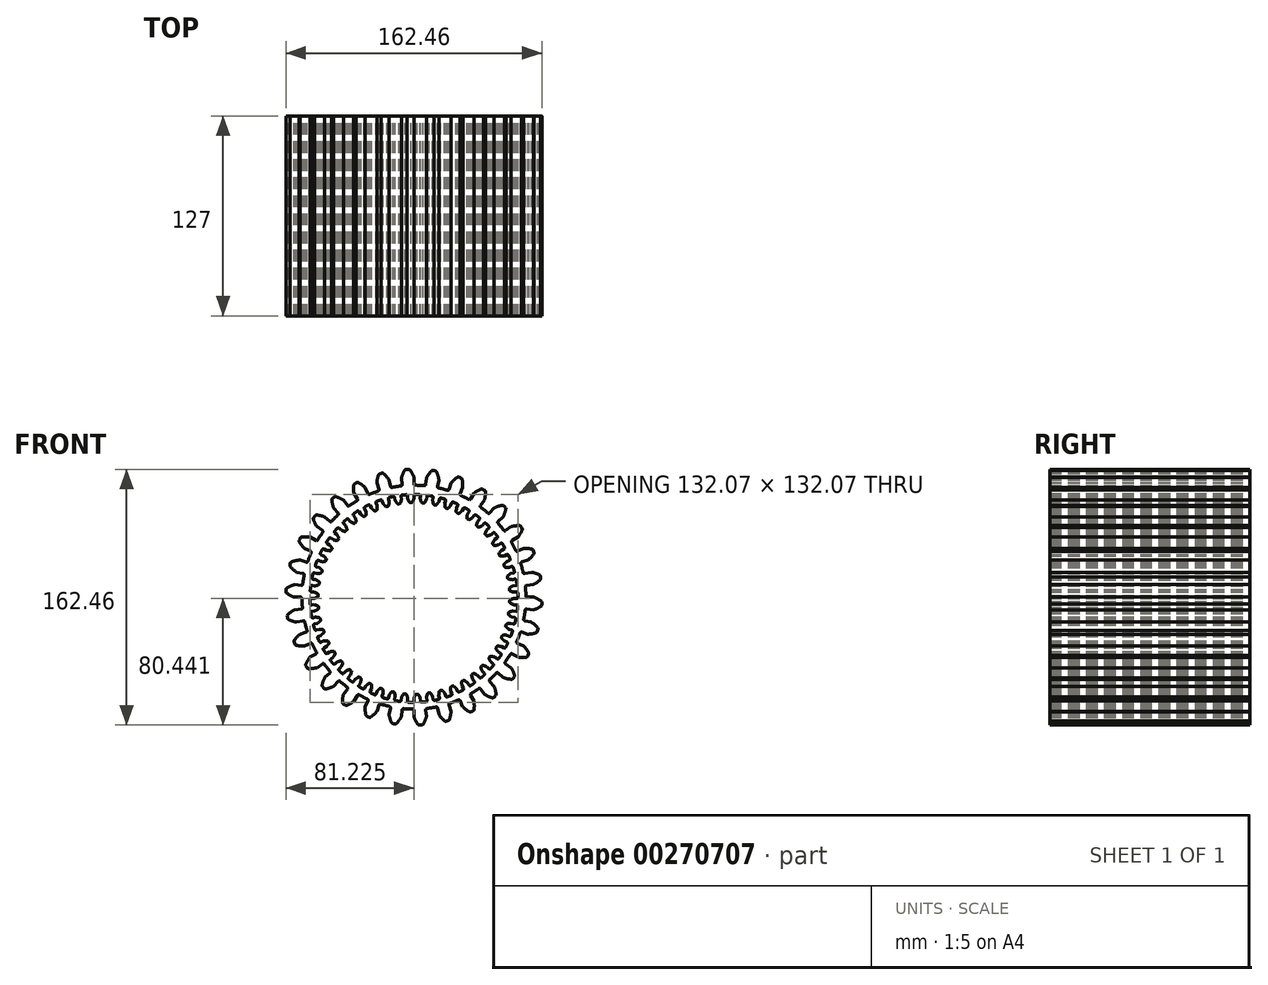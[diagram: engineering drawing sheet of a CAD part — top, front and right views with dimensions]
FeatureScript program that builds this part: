
annotation { "Feature Type Name" : "Feature", "Feature Type Description" : "" }
export const myFeature = defineFeature(function(context is Context, id is Id, definition is map)
    precondition{}
    {
        {
            var Q0;
            Q0=qCreatedBy(makeId("Front.planeOp"),FACE);
            var sketch = newSketch(context, id + "F0", { "sketchPlane" : qUnion([Q0])});
            skArc(sketch, "E0", {"start": v(-8.2, 70.64) * mm, "mid": v(-11.13, 70.24) * mm, "end": v(-14.02, 69.72) * mm});
            skArc(sketch, "E1.trimOffspring", {"start": v(0, 76.2) * mm, "mid": v(-1.16, 78.65) * mm, "end": v(-2.65, 80.92) * mm});
            skLineSegment(sketch, "E2", {"start": v(-3.27, 81.23) * mm, "end": v(-4.26, 81.23) * mm});
            skLineSegment(sketch, "E3", {"start": v(0, 76.2) * mm, "end": v(0, 71.9) * mm});
            skLineSegment(sketch, "E4.MirrorCS", {"start": v(-5.24, 81.13) * mm, "end": v(-4.26, 81.23) * mm});
            skArc(sketch, "E5.MirrorCS", {"start": v(-7.97, 75.78) * mm, "mid": v(-7.07, 78.34) * mm, "end": v(-5.83, 80.75) * mm});
            skLineSegment(sketch, "E6.MirrorCS", {"start": v(-7.97, 75.78) * mm, "end": v(-7.52, 71.5) * mm});
            skPoint(sketch, "E7.visualSharp", {"position": v(0, 71.12) * mm});
            skArc(sketch, "E7.filletArc", {"start": v(0, 71.9) * mm, "mid": v(0.23, 71.35) * mm, "end": v(0.78, 71.12) * mm});
            skPoint(sketch, "E8.visualSharp", {"position": v(-7.43, 70.73) * mm});
            skArc(sketch, "E8.filletArc", {"start": v(-8.2, 70.64) * mm, "mid": v(-7.68, 70.93) * mm, "end": v(-7.52, 71.5) * mm});
            skPoint(sketch, "E9.visualSharp", {"position": v(-5.62, 81.09) * mm});
            skArc(sketch, "E9.filletArc", {"start": v(-5.24, 81.13) * mm, "mid": v(-5.57, 81) * mm, "end": v(-5.83, 80.75) * mm});
            skPoint(sketch, "E10.visualSharp", {"position": v(-2.89, 81.23) * mm});
            skArc(sketch, "E10.filletArc", {"start": v(-2.65, 80.92) * mm, "mid": v(-2.92, 81.15) * mm, "end": v(-3.27, 81.23) * mm});
            skArc(sketch, "E11.1.0", {"start": v(-22.72, 67.4) * mm, "mid": v(-22.26, 67.79) * mm, "end": v(-22.22, 68.38) * mm});
            skLineSegment(sketch, "E11.1.1", {"start": v(-23.55, 72.47) * mm, "end": v(-22.22, 68.38) * mm});
            skArc(sketch, "E11.1.2", {"start": v(-23.55, 72.47) * mm, "mid": v(-23.2, 75.16) * mm, "end": v(-22.49, 77.78) * mm});
            skArc(sketch, "E11.1.3", {"start": v(-21.99, 78.26) * mm, "mid": v(-22.3, 78.08) * mm, "end": v(-22.49, 77.78) * mm});
            skLineSegment(sketch, "E11.1.4", {"start": v(-21.99, 78.26) * mm, "end": v(-21.05, 78.57) * mm});
            skLineSegment(sketch, "E11.1.5", {"start": v(-20.09, 78.77) * mm, "end": v(-21.05, 78.57) * mm});
            skArc(sketch, "E11.1.6", {"start": v(-19.41, 78.6) * mm, "mid": v(-19.73, 78.77) * mm, "end": v(-20.09, 78.77) * mm});
            skArc(sketch, "E11.1.7", {"start": v(-15.84, 74.53) * mm, "mid": v(-17.48, 76.7) * mm, "end": v(-19.41, 78.6) * mm});
            skLineSegment(sketch, "E11.1.8", {"start": v(-15.84, 74.53) * mm, "end": v(-14.95, 70.33) * mm});
            skArc(sketch, "E11.1.9", {"start": v(-14.95, 70.33) * mm, "mid": v(-14.61, 69.84) * mm, "end": v(-14.02, 69.72) * mm});
            skArc(sketch, "E11.2.0", {"start": v(-36.23, 61.2) * mm, "mid": v(-35.87, 61.68) * mm, "end": v(-35.95, 62.27) * mm});
            skLineSegment(sketch, "E11.2.1", {"start": v(-38.1, 66) * mm, "end": v(-35.95, 62.27) * mm});
            skArc(sketch, "E11.2.2", {"start": v(-38.1, 66) * mm, "mid": v(-38.33, 68.7) * mm, "end": v(-38.17, 71.4) * mm});
            skArc(sketch, "E11.2.3", {"start": v(-37.78, 71.98) * mm, "mid": v(-38.04, 71.74) * mm, "end": v(-38.17, 71.4) * mm});
            skLineSegment(sketch, "E11.2.4", {"start": v(-37.78, 71.98) * mm, "end": v(-36.93, 72.47) * mm});
            skLineSegment(sketch, "E11.2.5", {"start": v(-36.03, 72.87) * mm, "end": v(-36.93, 72.47) * mm});
            skArc(sketch, "E11.2.6", {"start": v(-35.33, 72.85) * mm, "mid": v(-35.68, 72.94) * mm, "end": v(-36.03, 72.87) * mm});
            skArc(sketch, "E11.2.7", {"start": v(-31, 69.61) * mm, "mid": v(-33.05, 71.38) * mm, "end": v(-35.33, 72.85) * mm});
            skLineSegment(sketch, "E11.2.8", {"start": v(-31, 69.61) * mm, "end": v(-29.25, 65.69) * mm});
            skArc(sketch, "E11.2.9", {"start": v(-29.25, 65.69) * mm, "mid": v(-28.81, 65.27) * mm, "end": v(-28.21, 65.28) * mm});
            skArc(sketch, "E11.3.0", {"start": v(-48.16, 52.33) * mm, "mid": v(-47.91, 52.87) * mm, "end": v(-48.11, 53.43) * mm});
            skLineSegment(sketch, "E11.3.1", {"start": v(-50.99, 56.63) * mm, "end": v(-48.11, 53.43) * mm});
            skArc(sketch, "E11.3.2", {"start": v(-50.99, 56.63) * mm, "mid": v(-51.77, 59.22) * mm, "end": v(-52.18, 61.9) * mm});
            skArc(sketch, "E11.3.3", {"start": v(-51.92, 62.55) * mm, "mid": v(-52.12, 62.26) * mm, "end": v(-52.18, 61.9) * mm});
            skLineSegment(sketch, "E11.3.4", {"start": v(-51.92, 62.55) * mm, "end": v(-51.19, 63.21) * mm});
            skLineSegment(sketch, "E11.3.5", {"start": v(-50.4, 63.8) * mm, "end": v(-51.19, 63.21) * mm});
            skArc(sketch, "E11.3.6", {"start": v(-49.7, 63.9) * mm, "mid": v(-50.06, 63.93) * mm, "end": v(-50.4, 63.8) * mm});
            skArc(sketch, "E11.3.7", {"start": v(-44.79, 61.65) * mm, "mid": v(-47.17, 62.95) * mm, "end": v(-49.7, 63.9) * mm});
            skLineSegment(sketch, "E11.3.8", {"start": v(-44.79, 61.65) * mm, "end": v(-42.26, 58.17) * mm});
            skArc(sketch, "E11.3.9", {"start": v(-42.26, 58.17) * mm, "mid": v(-41.75, 57.86) * mm, "end": v(-41.17, 58) * mm});
            skArc(sketch, "E11.4.0", {"start": v(-58, 41.17) * mm, "mid": v(-57.86, 41.75) * mm, "end": v(-58.17, 42.26) * mm});
            skLineSegment(sketch, "E11.4.1", {"start": v(-61.65, 44.79) * mm, "end": v(-58.17, 42.26) * mm});
            skArc(sketch, "E11.4.2", {"start": v(-61.65, 44.79) * mm, "mid": v(-62.95, 47.17) * mm, "end": v(-63.9, 49.7) * mm});
            skArc(sketch, "E11.4.3", {"start": v(-63.8, 50.4) * mm, "mid": v(-63.93, 50.06) * mm, "end": v(-63.9, 49.7) * mm});
            skLineSegment(sketch, "E11.4.4", {"start": v(-63.8, 50.4) * mm, "end": v(-63.21, 51.19) * mm});
            skLineSegment(sketch, "E11.4.5", {"start": v(-62.55, 51.92) * mm, "end": v(-63.21, 51.19) * mm});
            skArc(sketch, "E11.4.6", {"start": v(-61.9, 52.18) * mm, "mid": v(-62.26, 52.12) * mm, "end": v(-62.55, 51.92) * mm});
            skArc(sketch, "E11.4.7", {"start": v(-56.63, 50.99) * mm, "mid": v(-59.22, 51.77) * mm, "end": v(-61.9, 52.18) * mm});
            skLineSegment(sketch, "E11.4.8", {"start": v(-56.63, 50.99) * mm, "end": v(-53.43, 48.11) * mm});
            skArc(sketch, "E11.4.9", {"start": v(-53.43, 48.11) * mm, "mid": v(-52.87, 47.91) * mm, "end": v(-52.33, 48.16) * mm});
            skArc(sketch, "E11.5.0", {"start": v(-65.28, 28.21) * mm, "mid": v(-65.27, 28.81) * mm, "end": v(-65.69, 29.25) * mm});
            skLineSegment(sketch, "E11.5.1", {"start": v(-69.61, 31) * mm, "end": v(-65.69, 29.25) * mm});
            skArc(sketch, "E11.5.2", {"start": v(-69.61, 31) * mm, "mid": v(-71.38, 33.05) * mm, "end": v(-72.85, 35.33) * mm});
            skArc(sketch, "E11.5.3", {"start": v(-72.87, 36.03) * mm, "mid": v(-72.94, 35.68) * mm, "end": v(-72.85, 35.33) * mm});
            skLineSegment(sketch, "E11.5.4", {"start": v(-72.87, 36.03) * mm, "end": v(-72.47, 36.93) * mm});
            skLineSegment(sketch, "E11.5.5", {"start": v(-71.98, 37.78) * mm, "end": v(-72.47, 36.93) * mm});
            skArc(sketch, "E11.5.6", {"start": v(-71.4, 38.17) * mm, "mid": v(-71.74, 38.04) * mm, "end": v(-71.98, 37.78) * mm});
            skArc(sketch, "E11.5.7", {"start": v(-66, 38.1) * mm, "mid": v(-68.7, 38.33) * mm, "end": v(-71.4, 38.17) * mm});
            skLineSegment(sketch, "E11.5.8", {"start": v(-66, 38.1) * mm, "end": v(-62.27, 35.95) * mm});
            skArc(sketch, "E11.5.9", {"start": v(-62.27, 35.95) * mm, "mid": v(-61.68, 35.87) * mm, "end": v(-61.2, 36.23) * mm});
            skArc(sketch, "E11.6.0", {"start": v(-69.72, 14.02) * mm, "mid": v(-69.84, 14.61) * mm, "end": v(-70.33, 14.95) * mm});
            skLineSegment(sketch, "E11.6.1", {"start": v(-74.53, 15.84) * mm, "end": v(-70.33, 14.95) * mm});
            skArc(sketch, "E11.6.2", {"start": v(-74.53, 15.84) * mm, "mid": v(-76.7, 17.48) * mm, "end": v(-78.6, 19.41) * mm});
            skArc(sketch, "E11.6.3", {"start": v(-78.77, 20.09) * mm, "mid": v(-78.77, 19.73) * mm, "end": v(-78.6, 19.41) * mm});
            skLineSegment(sketch, "E11.6.4", {"start": v(-78.77, 20.09) * mm, "end": v(-78.57, 21.05) * mm});
            skLineSegment(sketch, "E11.6.5", {"start": v(-78.26, 21.99) * mm, "end": v(-78.57, 21.05) * mm});
            skArc(sketch, "E11.6.6", {"start": v(-77.78, 22.49) * mm, "mid": v(-78.08, 22.3) * mm, "end": v(-78.26, 21.99) * mm});
            skArc(sketch, "E11.6.7", {"start": v(-72.47, 23.55) * mm, "mid": v(-75.16, 23.2) * mm, "end": v(-77.78, 22.49) * mm});
            skLineSegment(sketch, "E11.6.8", {"start": v(-72.47, 23.55) * mm, "end": v(-68.38, 22.22) * mm});
            skArc(sketch, "E11.6.9", {"start": v(-68.38, 22.22) * mm, "mid": v(-67.79, 22.26) * mm, "end": v(-67.4, 22.72) * mm});
            skArc(sketch, "E11.7.0", {"start": v(-71.12, -0.78) * mm, "mid": v(-71.35, -0.23) * mm, "end": v(-71.9, 0) * mm});
            skLineSegment(sketch, "E11.7.1", {"start": v(-76.2, 0) * mm, "end": v(-71.9, 0) * mm});
            skArc(sketch, "E11.7.2", {"start": v(-76.2, 0) * mm, "mid": v(-78.65, 1.16) * mm, "end": v(-80.92, 2.65) * mm});
            skArc(sketch, "E11.7.3", {"start": v(-81.23, 3.27) * mm, "mid": v(-81.15, 2.92) * mm, "end": v(-80.92, 2.65) * mm});
            skLineSegment(sketch, "E11.7.4", {"start": v(-81.23, 3.27) * mm, "end": v(-81.23, 4.26) * mm});
            skLineSegment(sketch, "E11.7.5", {"start": v(-81.13, 5.24) * mm, "end": v(-81.23, 4.26) * mm});
            skArc(sketch, "E11.7.6", {"start": v(-80.75, 5.83) * mm, "mid": v(-81, 5.57) * mm, "end": v(-81.13, 5.24) * mm});
            skArc(sketch, "E11.7.7", {"start": v(-75.78, 7.97) * mm, "mid": v(-78.34, 7.07) * mm, "end": v(-80.75, 5.83) * mm});
            skLineSegment(sketch, "E11.7.8", {"start": v(-75.78, 7.97) * mm, "end": v(-71.5, 7.52) * mm});
            skArc(sketch, "E11.7.9", {"start": v(-71.5, 7.52) * mm, "mid": v(-70.93, 7.68) * mm, "end": v(-70.64, 8.2) * mm});
            skArc(sketch, "E11.8.0", {"start": v(-69.4, -15.55) * mm, "mid": v(-69.74, -15.06) * mm, "end": v(-70.33, -14.95) * mm});
            skLineSegment(sketch, "E11.8.1", {"start": v(-74.53, -15.84) * mm, "end": v(-70.33, -14.95) * mm});
            skArc(sketch, "E11.8.2", {"start": v(-74.53, -15.84) * mm, "mid": v(-77.18, -15.22) * mm, "end": v(-79.7, -14.23) * mm});
            skArc(sketch, "E11.8.3", {"start": v(-80.13, -13.69) * mm, "mid": v(-79.98, -14.01) * mm, "end": v(-79.7, -14.23) * mm});
            skLineSegment(sketch, "E11.8.4", {"start": v(-80.13, -13.69) * mm, "end": v(-80.34, -12.72) * mm});
            skLineSegment(sketch, "E11.8.5", {"start": v(-80.44, -11.75) * mm, "end": v(-80.34, -12.72) * mm});
            skArc(sketch, "E11.8.6", {"start": v(-80.2, -11.1) * mm, "mid": v(-80.4, -11.4) * mm, "end": v(-80.44, -11.75) * mm});
            skArc(sketch, "E11.8.7", {"start": v(-75.78, -7.97) * mm, "mid": v(-78.1, -9.37) * mm, "end": v(-80.2, -11.1) * mm});
            skLineSegment(sketch, "E11.8.8", {"start": v(-75.78, -7.97) * mm, "end": v(-71.5, -7.52) * mm});
            skArc(sketch, "E11.8.9", {"start": v(-71.5, -7.52) * mm, "mid": v(-70.98, -7.23) * mm, "end": v(-70.8, -6.66) * mm});
            skArc(sketch, "E11.9.0", {"start": v(-64.65, -29.64) * mm, "mid": v(-65.09, -29.23) * mm, "end": v(-65.69, -29.25) * mm});
            skLineSegment(sketch, "E11.9.1", {"start": v(-69.61, -31) * mm, "end": v(-65.69, -29.25) * mm});
            skArc(sketch, "E11.9.2", {"start": v(-69.61, -31) * mm, "mid": v(-72.32, -30.94) * mm, "end": v(-75, -30.5) * mm});
            skArc(sketch, "E11.9.3", {"start": v(-75.54, -30.05) * mm, "mid": v(-75.32, -30.33) * mm, "end": v(-75, -30.5) * mm});
            skLineSegment(sketch, "E11.9.4", {"start": v(-75.54, -30.05) * mm, "end": v(-75.94, -29.15) * mm});
            skLineSegment(sketch, "E11.9.5", {"start": v(-76.24, -28.21) * mm, "end": v(-75.94, -29.15) * mm});
            skArc(sketch, "E11.9.6", {"start": v(-76.14, -27.52) * mm, "mid": v(-76.27, -27.86) * mm, "end": v(-76.24, -28.21) * mm});
            skArc(sketch, "E11.9.7", {"start": v(-72.47, -23.55) * mm, "mid": v(-74.45, -25.4) * mm, "end": v(-76.14, -27.52) * mm});
            skLineSegment(sketch, "E11.9.8", {"start": v(-72.47, -23.55) * mm, "end": v(-68.38, -22.22) * mm});
            skArc(sketch, "E11.9.9", {"start": v(-68.38, -22.22) * mm, "mid": v(-67.93, -21.83) * mm, "end": v(-67.88, -21.24) * mm});
            skArc(sketch, "E11.10.0", {"start": v(-57.08, -42.43) * mm, "mid": v(-57.59, -42.12) * mm, "end": v(-58.17, -42.26) * mm});
            skLineSegment(sketch, "E11.10.1", {"start": v(-61.65, -44.79) * mm, "end": v(-58.17, -42.26) * mm});
            skArc(sketch, "E11.10.2", {"start": v(-61.65, -44.79) * mm, "mid": v(-64.31, -45.3) * mm, "end": v(-67.02, -45.42) * mm});
            skArc(sketch, "E11.10.3", {"start": v(-67.64, -45.1) * mm, "mid": v(-67.37, -45.33) * mm, "end": v(-67.02, -45.42) * mm});
            skLineSegment(sketch, "E11.10.4", {"start": v(-67.64, -45.1) * mm, "end": v(-68.22, -44.3) * mm});
            skLineSegment(sketch, "E11.10.5", {"start": v(-68.7, -43.45) * mm, "end": v(-68.22, -44.3) * mm});
            skArc(sketch, "E11.10.6", {"start": v(-68.75, -42.75) * mm, "mid": v(-68.81, -43.1) * mm, "end": v(-68.7, -43.45) * mm});
            skArc(sketch, "E11.10.7", {"start": v(-66, -38.1) * mm, "mid": v(-67.54, -40.33) * mm, "end": v(-68.75, -42.75) * mm});
            skLineSegment(sketch, "E11.10.8", {"start": v(-66, -38.1) * mm, "end": v(-62.27, -35.95) * mm});
            skArc(sketch, "E11.10.9", {"start": v(-62.27, -35.95) * mm, "mid": v(-61.9, -35.48) * mm, "end": v(-61.98, -34.88) * mm});
            skArc(sketch, "E11.11.0", {"start": v(-47, -53.37) * mm, "mid": v(-47.57, -53.18) * mm, "end": v(-48.11, -53.43) * mm});
            skLineSegment(sketch, "E11.11.1", {"start": v(-50.99, -56.63) * mm, "end": v(-48.11, -53.43) * mm});
            skArc(sketch, "E11.11.2", {"start": v(-50.99, -56.63) * mm, "mid": v(-53.49, -57.68) * mm, "end": v(-56.11, -58.36) * mm});
            skArc(sketch, "E11.11.3", {"start": v(-56.78, -58.17) * mm, "mid": v(-56.47, -58.35) * mm, "end": v(-56.11, -58.36) * mm});
            skLineSegment(sketch, "E11.11.4", {"start": v(-56.78, -58.17) * mm, "end": v(-57.52, -57.52) * mm});
            skLineSegment(sketch, "E11.11.5", {"start": v(-58.17, -56.78) * mm, "end": v(-57.52, -57.52) * mm});
            skArc(sketch, "E11.11.6", {"start": v(-58.36, -56.11) * mm, "mid": v(-58.35, -56.47) * mm, "end": v(-58.17, -56.78) * mm});
            skArc(sketch, "E11.11.7", {"start": v(-56.63, -50.99) * mm, "mid": v(-57.68, -53.49) * mm, "end": v(-58.36, -56.11) * mm});
            skLineSegment(sketch, "E11.11.8", {"start": v(-56.63, -50.99) * mm, "end": v(-53.43, -48.11) * mm});
            skArc(sketch, "E11.11.9", {"start": v(-53.43, -48.11) * mm, "mid": v(-53.18, -47.57) * mm, "end": v(-53.37, -47) * mm});
            skArc(sketch, "E11.12.0", {"start": v(-34.88, -61.98) * mm, "mid": v(-35.48, -61.9) * mm, "end": v(-35.95, -62.27) * mm});
            skLineSegment(sketch, "E11.12.1", {"start": v(-38.1, -66) * mm, "end": v(-35.95, -62.27) * mm});
            skArc(sketch, "E11.12.2", {"start": v(-38.1, -66) * mm, "mid": v(-40.33, -67.54) * mm, "end": v(-42.75, -68.75) * mm});
            skArc(sketch, "E11.12.3", {"start": v(-43.45, -68.7) * mm, "mid": v(-43.1, -68.81) * mm, "end": v(-42.75, -68.75) * mm});
            skLineSegment(sketch, "E11.12.4", {"start": v(-43.45, -68.7) * mm, "end": v(-44.3, -68.22) * mm});
            skLineSegment(sketch, "E11.12.5", {"start": v(-45.1, -67.64) * mm, "end": v(-44.3, -68.22) * mm});
            skArc(sketch, "E11.12.6", {"start": v(-45.42, -67.02) * mm, "mid": v(-45.33, -67.37) * mm, "end": v(-45.1, -67.64) * mm});
            skArc(sketch, "E11.12.7", {"start": v(-44.79, -61.65) * mm, "mid": v(-45.3, -64.31) * mm, "end": v(-45.42, -67.02) * mm});
            skLineSegment(sketch, "E11.12.8", {"start": v(-44.79, -61.65) * mm, "end": v(-42.26, -58.17) * mm});
            skArc(sketch, "E11.12.9", {"start": v(-42.26, -58.17) * mm, "mid": v(-42.12, -57.59) * mm, "end": v(-42.43, -57.08) * mm});
            skArc(sketch, "E11.13.0", {"start": v(-21.24, -67.88) * mm, "mid": v(-21.83, -67.93) * mm, "end": v(-22.22, -68.38) * mm});
            skLineSegment(sketch, "E11.13.1", {"start": v(-23.55, -72.47) * mm, "end": v(-22.22, -68.38) * mm});
            skArc(sketch, "E11.13.2", {"start": v(-23.55, -72.47) * mm, "mid": v(-25.4, -74.45) * mm, "end": v(-27.52, -76.14) * mm});
            skArc(sketch, "E11.13.3", {"start": v(-28.21, -76.24) * mm, "mid": v(-27.86, -76.27) * mm, "end": v(-27.52, -76.14) * mm});
            skLineSegment(sketch, "E11.13.4", {"start": v(-28.21, -76.24) * mm, "end": v(-29.15, -75.94) * mm});
            skLineSegment(sketch, "E11.13.5", {"start": v(-30.05, -75.54) * mm, "end": v(-29.15, -75.94) * mm});
            skArc(sketch, "E11.13.6", {"start": v(-30.5, -75) * mm, "mid": v(-30.33, -75.32) * mm, "end": v(-30.05, -75.54) * mm});
            skArc(sketch, "E11.13.7", {"start": v(-31, -69.61) * mm, "mid": v(-30.94, -72.32) * mm, "end": v(-30.5, -75) * mm});
            skLineSegment(sketch, "E11.13.8", {"start": v(-31, -69.61) * mm, "end": v(-29.25, -65.69) * mm});
            skArc(sketch, "E11.13.9", {"start": v(-29.25, -65.69) * mm, "mid": v(-29.23, -65.09) * mm, "end": v(-29.64, -64.65) * mm});
            skArc(sketch, "E11.14.0", {"start": v(-6.66, -70.8) * mm, "mid": v(-7.23, -70.98) * mm, "end": v(-7.52, -71.5) * mm});
            skLineSegment(sketch, "E11.14.1", {"start": v(-7.97, -75.78) * mm, "end": v(-7.52, -71.5) * mm});
            skArc(sketch, "E11.14.2", {"start": v(-7.97, -75.78) * mm, "mid": v(-9.37, -78.1) * mm, "end": v(-11.1, -80.2) * mm});
            skArc(sketch, "E11.14.3", {"start": v(-11.75, -80.44) * mm, "mid": v(-11.4, -80.4) * mm, "end": v(-11.1, -80.2) * mm});
            skLineSegment(sketch, "E11.14.4", {"start": v(-11.75, -80.44) * mm, "end": v(-12.72, -80.34) * mm});
            skLineSegment(sketch, "E11.14.5", {"start": v(-13.69, -80.13) * mm, "end": v(-12.72, -80.34) * mm});
            skArc(sketch, "E11.14.6", {"start": v(-14.23, -79.7) * mm, "mid": v(-14.01, -79.98) * mm, "end": v(-13.69, -80.13) * mm});
            skArc(sketch, "E11.14.7", {"start": v(-15.84, -74.53) * mm, "mid": v(-15.22, -77.18) * mm, "end": v(-14.23, -79.7) * mm});
            skLineSegment(sketch, "E11.14.8", {"start": v(-15.84, -74.53) * mm, "end": v(-14.95, -70.33) * mm});
            skArc(sketch, "E11.14.9", {"start": v(-14.95, -70.33) * mm, "mid": v(-15.06, -69.74) * mm, "end": v(-15.55, -69.4) * mm});
            skArc(sketch, "E11.15.0", {"start": v(8.2, -70.64) * mm, "mid": v(7.68, -70.93) * mm, "end": v(7.52, -71.5) * mm});
            skLineSegment(sketch, "E11.15.1", {"start": v(7.97, -75.78) * mm, "end": v(7.52, -71.5) * mm});
            skArc(sketch, "E11.15.2", {"start": v(7.97, -75.78) * mm, "mid": v(7.07, -78.34) * mm, "end": v(5.83, -80.75) * mm});
            skArc(sketch, "E11.15.3", {"start": v(5.24, -81.13) * mm, "mid": v(5.57, -81) * mm, "end": v(5.83, -80.75) * mm});
            skLineSegment(sketch, "E11.15.4", {"start": v(5.24, -81.13) * mm, "end": v(4.26, -81.23) * mm});
            skLineSegment(sketch, "E11.15.5", {"start": v(3.27, -81.23) * mm, "end": v(4.26, -81.23) * mm});
            skArc(sketch, "E11.15.6", {"start": v(2.65, -80.92) * mm, "mid": v(2.92, -81.15) * mm, "end": v(3.27, -81.23) * mm});
            skArc(sketch, "E11.15.7", {"start": v(0, -76.2) * mm, "mid": v(1.16, -78.65) * mm, "end": v(2.65, -80.92) * mm});
            skLineSegment(sketch, "E11.15.8", {"start": v(0, -76.2) * mm, "end": v(0, -71.9) * mm});
            skArc(sketch, "E11.15.9", {"start": v(0, -71.9) * mm, "mid": v(-0.23, -71.35) * mm, "end": v(-0.78, -71.12) * mm});
            skArc(sketch, "E11.16.0", {"start": v(22.72, -67.4) * mm, "mid": v(22.26, -67.79) * mm, "end": v(22.22, -68.38) * mm});
            skLineSegment(sketch, "E11.16.1", {"start": v(23.55, -72.47) * mm, "end": v(22.22, -68.38) * mm});
            skArc(sketch, "E11.16.2", {"start": v(23.55, -72.47) * mm, "mid": v(23.2, -75.16) * mm, "end": v(22.49, -77.78) * mm});
            skArc(sketch, "E11.16.3", {"start": v(21.99, -78.26) * mm, "mid": v(22.3, -78.08) * mm, "end": v(22.49, -77.78) * mm});
            skLineSegment(sketch, "E11.16.4", {"start": v(21.99, -78.26) * mm, "end": v(21.05, -78.57) * mm});
            skLineSegment(sketch, "E11.16.5", {"start": v(20.09, -78.77) * mm, "end": v(21.05, -78.57) * mm});
            skArc(sketch, "E11.16.6", {"start": v(19.41, -78.6) * mm, "mid": v(19.73, -78.77) * mm, "end": v(20.09, -78.77) * mm});
            skArc(sketch, "E11.16.7", {"start": v(15.84, -74.53) * mm, "mid": v(17.48, -76.7) * mm, "end": v(19.41, -78.6) * mm});
            skLineSegment(sketch, "E11.16.8", {"start": v(15.84, -74.53) * mm, "end": v(14.95, -70.33) * mm});
            skArc(sketch, "E11.16.9", {"start": v(14.95, -70.33) * mm, "mid": v(14.61, -69.84) * mm, "end": v(14.02, -69.72) * mm});
            skArc(sketch, "E11.17.0", {"start": v(36.23, -61.2) * mm, "mid": v(35.87, -61.68) * mm, "end": v(35.95, -62.27) * mm});
            skLineSegment(sketch, "E11.17.1", {"start": v(38.1, -66) * mm, "end": v(35.95, -62.27) * mm});
            skArc(sketch, "E11.17.2", {"start": v(38.1, -66) * mm, "mid": v(38.33, -68.7) * mm, "end": v(38.17, -71.4) * mm});
            skArc(sketch, "E11.17.3", {"start": v(37.78, -71.98) * mm, "mid": v(38.04, -71.74) * mm, "end": v(38.17, -71.4) * mm});
            skLineSegment(sketch, "E11.17.4", {"start": v(37.78, -71.98) * mm, "end": v(36.93, -72.47) * mm});
            skLineSegment(sketch, "E11.17.5", {"start": v(36.03, -72.87) * mm, "end": v(36.93, -72.47) * mm});
            skArc(sketch, "E11.17.6", {"start": v(35.33, -72.85) * mm, "mid": v(35.68, -72.94) * mm, "end": v(36.03, -72.87) * mm});
            skArc(sketch, "E11.17.7", {"start": v(31, -69.61) * mm, "mid": v(33.05, -71.38) * mm, "end": v(35.33, -72.85) * mm});
            skLineSegment(sketch, "E11.17.8", {"start": v(31, -69.61) * mm, "end": v(29.25, -65.69) * mm});
            skArc(sketch, "E11.17.9", {"start": v(29.25, -65.69) * mm, "mid": v(28.81, -65.27) * mm, "end": v(28.21, -65.28) * mm});
            skArc(sketch, "E11.18.0", {"start": v(48.16, -52.33) * mm, "mid": v(47.91, -52.87) * mm, "end": v(48.11, -53.43) * mm});
            skLineSegment(sketch, "E11.18.1", {"start": v(50.99, -56.63) * mm, "end": v(48.11, -53.43) * mm});
            skArc(sketch, "E11.18.2", {"start": v(50.99, -56.63) * mm, "mid": v(51.77, -59.22) * mm, "end": v(52.18, -61.9) * mm});
            skArc(sketch, "E11.18.3", {"start": v(51.92, -62.55) * mm, "mid": v(52.12, -62.26) * mm, "end": v(52.18, -61.9) * mm});
            skLineSegment(sketch, "E11.18.4", {"start": v(51.92, -62.55) * mm, "end": v(51.19, -63.21) * mm});
            skLineSegment(sketch, "E11.18.5", {"start": v(50.4, -63.8) * mm, "end": v(51.19, -63.21) * mm});
            skArc(sketch, "E11.18.6", {"start": v(49.7, -63.9) * mm, "mid": v(50.06, -63.93) * mm, "end": v(50.4, -63.8) * mm});
            skArc(sketch, "E11.18.7", {"start": v(44.79, -61.65) * mm, "mid": v(47.17, -62.95) * mm, "end": v(49.7, -63.9) * mm});
            skLineSegment(sketch, "E11.18.8", {"start": v(44.79, -61.65) * mm, "end": v(42.26, -58.17) * mm});
            skArc(sketch, "E11.18.9", {"start": v(42.26, -58.17) * mm, "mid": v(41.75, -57.86) * mm, "end": v(41.17, -58) * mm});
            skArc(sketch, "E11.19.0", {"start": v(58, -41.17) * mm, "mid": v(57.86, -41.75) * mm, "end": v(58.17, -42.26) * mm});
            skLineSegment(sketch, "E11.19.1", {"start": v(61.65, -44.79) * mm, "end": v(58.17, -42.26) * mm});
            skArc(sketch, "E11.19.2", {"start": v(61.65, -44.79) * mm, "mid": v(62.95, -47.17) * mm, "end": v(63.9, -49.7) * mm});
            skArc(sketch, "E11.19.3", {"start": v(63.8, -50.4) * mm, "mid": v(63.93, -50.06) * mm, "end": v(63.9, -49.7) * mm});
            skLineSegment(sketch, "E11.19.4", {"start": v(63.8, -50.4) * mm, "end": v(63.21, -51.19) * mm});
            skLineSegment(sketch, "E11.19.5", {"start": v(62.55, -51.92) * mm, "end": v(63.21, -51.19) * mm});
            skArc(sketch, "E11.19.6", {"start": v(61.9, -52.18) * mm, "mid": v(62.26, -52.12) * mm, "end": v(62.55, -51.92) * mm});
            skArc(sketch, "E11.19.7", {"start": v(56.63, -50.99) * mm, "mid": v(59.22, -51.77) * mm, "end": v(61.9, -52.18) * mm});
            skLineSegment(sketch, "E11.19.8", {"start": v(56.63, -50.99) * mm, "end": v(53.43, -48.11) * mm});
            skArc(sketch, "E11.19.9", {"start": v(53.43, -48.11) * mm, "mid": v(52.87, -47.91) * mm, "end": v(52.33, -48.16) * mm});
            skArc(sketch, "E11.20.0", {"start": v(65.28, -28.21) * mm, "mid": v(65.27, -28.81) * mm, "end": v(65.69, -29.25) * mm});
            skLineSegment(sketch, "E11.20.1", {"start": v(69.61, -31) * mm, "end": v(65.69, -29.25) * mm});
            skArc(sketch, "E11.20.2", {"start": v(69.61, -31) * mm, "mid": v(71.38, -33.05) * mm, "end": v(72.85, -35.33) * mm});
            skArc(sketch, "E11.20.3", {"start": v(72.87, -36.03) * mm, "mid": v(72.94, -35.68) * mm, "end": v(72.85, -35.33) * mm});
            skLineSegment(sketch, "E11.20.4", {"start": v(72.87, -36.03) * mm, "end": v(72.47, -36.93) * mm});
            skLineSegment(sketch, "E11.20.5", {"start": v(71.98, -37.78) * mm, "end": v(72.47, -36.93) * mm});
            skArc(sketch, "E11.20.6", {"start": v(71.4, -38.17) * mm, "mid": v(71.74, -38.04) * mm, "end": v(71.98, -37.78) * mm});
            skArc(sketch, "E11.20.7", {"start": v(66, -38.1) * mm, "mid": v(68.7, -38.33) * mm, "end": v(71.4, -38.17) * mm});
            skLineSegment(sketch, "E11.20.8", {"start": v(66, -38.1) * mm, "end": v(62.27, -35.95) * mm});
            skArc(sketch, "E11.20.9", {"start": v(62.27, -35.95) * mm, "mid": v(61.68, -35.87) * mm, "end": v(61.2, -36.23) * mm});
            skArc(sketch, "E11.21.0", {"start": v(69.72, -14.02) * mm, "mid": v(69.84, -14.61) * mm, "end": v(70.33, -14.95) * mm});
            skLineSegment(sketch, "E11.21.1", {"start": v(74.53, -15.84) * mm, "end": v(70.33, -14.95) * mm});
            skArc(sketch, "E11.21.2", {"start": v(74.53, -15.84) * mm, "mid": v(76.7, -17.48) * mm, "end": v(78.6, -19.41) * mm});
            skArc(sketch, "E11.21.3", {"start": v(78.77, -20.09) * mm, "mid": v(78.77, -19.73) * mm, "end": v(78.6, -19.41) * mm});
            skLineSegment(sketch, "E11.21.4", {"start": v(78.77, -20.09) * mm, "end": v(78.57, -21.05) * mm});
            skLineSegment(sketch, "E11.21.5", {"start": v(78.26, -21.99) * mm, "end": v(78.57, -21.05) * mm});
            skArc(sketch, "E11.21.6", {"start": v(77.78, -22.49) * mm, "mid": v(78.08, -22.3) * mm, "end": v(78.26, -21.99) * mm});
            skArc(sketch, "E11.21.7", {"start": v(72.47, -23.55) * mm, "mid": v(75.16, -23.2) * mm, "end": v(77.78, -22.49) * mm});
            skLineSegment(sketch, "E11.21.8", {"start": v(72.47, -23.55) * mm, "end": v(68.38, -22.22) * mm});
            skArc(sketch, "E11.21.9", {"start": v(68.38, -22.22) * mm, "mid": v(67.79, -22.26) * mm, "end": v(67.4, -22.72) * mm});
            skArc(sketch, "E11.22.0", {"start": v(71.12, 0.78) * mm, "mid": v(71.35, 0.23) * mm, "end": v(71.9, 0) * mm});
            skLineSegment(sketch, "E11.22.1", {"start": v(76.2, 0) * mm, "end": v(71.9, 0) * mm});
            skArc(sketch, "E11.22.2", {"start": v(76.2, 0) * mm, "mid": v(78.65, -1.16) * mm, "end": v(80.92, -2.65) * mm});
            skArc(sketch, "E11.22.3", {"start": v(81.23, -3.27) * mm, "mid": v(81.15, -2.92) * mm, "end": v(80.92, -2.65) * mm});
            skLineSegment(sketch, "E11.22.4", {"start": v(81.23, -3.27) * mm, "end": v(81.23, -4.26) * mm});
            skLineSegment(sketch, "E11.22.5", {"start": v(81.13, -5.24) * mm, "end": v(81.23, -4.26) * mm});
            skArc(sketch, "E11.22.6", {"start": v(80.75, -5.83) * mm, "mid": v(81, -5.57) * mm, "end": v(81.13, -5.24) * mm});
            skArc(sketch, "E11.22.7", {"start": v(75.78, -7.97) * mm, "mid": v(78.34, -7.07) * mm, "end": v(80.75, -5.83) * mm});
            skLineSegment(sketch, "E11.22.8", {"start": v(75.78, -7.97) * mm, "end": v(71.5, -7.52) * mm});
            skArc(sketch, "E11.22.9", {"start": v(71.5, -7.52) * mm, "mid": v(70.93, -7.68) * mm, "end": v(70.64, -8.2) * mm});
            skArc(sketch, "E11.23.0", {"start": v(69.4, 15.55) * mm, "mid": v(69.74, 15.06) * mm, "end": v(70.33, 14.95) * mm});
            skLineSegment(sketch, "E11.23.1", {"start": v(74.53, 15.84) * mm, "end": v(70.33, 14.95) * mm});
            skArc(sketch, "E11.23.2", {"start": v(74.53, 15.84) * mm, "mid": v(77.18, 15.22) * mm, "end": v(79.7, 14.23) * mm});
            skArc(sketch, "E11.23.3", {"start": v(80.13, 13.69) * mm, "mid": v(79.98, 14.01) * mm, "end": v(79.7, 14.23) * mm});
            skLineSegment(sketch, "E11.23.4", {"start": v(80.13, 13.69) * mm, "end": v(80.34, 12.72) * mm});
            skLineSegment(sketch, "E11.23.5", {"start": v(80.44, 11.75) * mm, "end": v(80.34, 12.72) * mm});
            skArc(sketch, "E11.23.6", {"start": v(80.2, 11.1) * mm, "mid": v(80.4, 11.4) * mm, "end": v(80.44, 11.75) * mm});
            skArc(sketch, "E11.23.7", {"start": v(75.78, 7.97) * mm, "mid": v(78.1, 9.37) * mm, "end": v(80.2, 11.1) * mm});
            skLineSegment(sketch, "E11.23.8", {"start": v(75.78, 7.97) * mm, "end": v(71.5, 7.52) * mm});
            skArc(sketch, "E11.23.9", {"start": v(71.5, 7.52) * mm, "mid": v(70.98, 7.23) * mm, "end": v(70.8, 6.66) * mm});
            skArc(sketch, "E11.24.0", {"start": v(64.65, 29.64) * mm, "mid": v(65.09, 29.23) * mm, "end": v(65.69, 29.25) * mm});
            skLineSegment(sketch, "E11.24.1", {"start": v(69.61, 31) * mm, "end": v(65.69, 29.25) * mm});
            skArc(sketch, "E11.24.2", {"start": v(69.61, 31) * mm, "mid": v(72.32, 30.94) * mm, "end": v(75, 30.5) * mm});
            skArc(sketch, "E11.24.3", {"start": v(75.54, 30.05) * mm, "mid": v(75.32, 30.33) * mm, "end": v(75, 30.5) * mm});
            skLineSegment(sketch, "E11.24.4", {"start": v(75.54, 30.05) * mm, "end": v(75.94, 29.15) * mm});
            skLineSegment(sketch, "E11.24.5", {"start": v(76.24, 28.21) * mm, "end": v(75.94, 29.15) * mm});
            skArc(sketch, "E11.24.6", {"start": v(76.14, 27.52) * mm, "mid": v(76.27, 27.86) * mm, "end": v(76.24, 28.21) * mm});
            skArc(sketch, "E11.24.7", {"start": v(72.47, 23.55) * mm, "mid": v(74.45, 25.4) * mm, "end": v(76.14, 27.52) * mm});
            skLineSegment(sketch, "E11.24.8", {"start": v(72.47, 23.55) * mm, "end": v(68.38, 22.22) * mm});
            skArc(sketch, "E11.24.9", {"start": v(68.38, 22.22) * mm, "mid": v(67.93, 21.83) * mm, "end": v(67.88, 21.24) * mm});
            skArc(sketch, "E11.25.0", {"start": v(57.08, 42.43) * mm, "mid": v(57.59, 42.12) * mm, "end": v(58.17, 42.26) * mm});
            skLineSegment(sketch, "E11.25.1", {"start": v(61.65, 44.79) * mm, "end": v(58.17, 42.26) * mm});
            skArc(sketch, "E11.25.2", {"start": v(61.65, 44.79) * mm, "mid": v(64.31, 45.3) * mm, "end": v(67.02, 45.42) * mm});
            skArc(sketch, "E11.25.3", {"start": v(67.64, 45.1) * mm, "mid": v(67.37, 45.33) * mm, "end": v(67.02, 45.42) * mm});
            skLineSegment(sketch, "E11.25.4", {"start": v(67.64, 45.1) * mm, "end": v(68.22, 44.3) * mm});
            skLineSegment(sketch, "E11.25.5", {"start": v(68.7, 43.45) * mm, "end": v(68.22, 44.3) * mm});
            skArc(sketch, "E11.25.6", {"start": v(68.75, 42.75) * mm, "mid": v(68.81, 43.1) * mm, "end": v(68.7, 43.45) * mm});
            skArc(sketch, "E11.25.7", {"start": v(66, 38.1) * mm, "mid": v(67.54, 40.33) * mm, "end": v(68.75, 42.75) * mm});
            skLineSegment(sketch, "E11.25.8", {"start": v(66, 38.1) * mm, "end": v(62.27, 35.95) * mm});
            skArc(sketch, "E11.25.9", {"start": v(62.27, 35.95) * mm, "mid": v(61.9, 35.48) * mm, "end": v(61.98, 34.88) * mm});
            skArc(sketch, "E11.26.0", {"start": v(47, 53.37) * mm, "mid": v(47.57, 53.18) * mm, "end": v(48.11, 53.43) * mm});
            skLineSegment(sketch, "E11.26.1", {"start": v(50.99, 56.63) * mm, "end": v(48.11, 53.43) * mm});
            skArc(sketch, "E11.26.2", {"start": v(50.99, 56.63) * mm, "mid": v(53.49, 57.68) * mm, "end": v(56.11, 58.36) * mm});
            skArc(sketch, "E11.26.3", {"start": v(56.78, 58.17) * mm, "mid": v(56.47, 58.35) * mm, "end": v(56.11, 58.36) * mm});
            skLineSegment(sketch, "E11.26.4", {"start": v(56.78, 58.17) * mm, "end": v(57.52, 57.52) * mm});
            skLineSegment(sketch, "E11.26.5", {"start": v(58.17, 56.78) * mm, "end": v(57.52, 57.52) * mm});
            skArc(sketch, "E11.26.6", {"start": v(58.36, 56.11) * mm, "mid": v(58.35, 56.47) * mm, "end": v(58.17, 56.78) * mm});
            skArc(sketch, "E11.26.7", {"start": v(56.63, 50.99) * mm, "mid": v(57.68, 53.49) * mm, "end": v(58.36, 56.11) * mm});
            skLineSegment(sketch, "E11.26.8", {"start": v(56.63, 50.99) * mm, "end": v(53.43, 48.11) * mm});
            skArc(sketch, "E11.26.9", {"start": v(53.43, 48.11) * mm, "mid": v(53.18, 47.57) * mm, "end": v(53.37, 47) * mm});
            skArc(sketch, "E11.27.0", {"start": v(34.88, 61.98) * mm, "mid": v(35.48, 61.9) * mm, "end": v(35.95, 62.27) * mm});
            skLineSegment(sketch, "E11.27.1", {"start": v(38.1, 66) * mm, "end": v(35.95, 62.27) * mm});
            skArc(sketch, "E11.27.2", {"start": v(38.1, 66) * mm, "mid": v(40.33, 67.54) * mm, "end": v(42.75, 68.75) * mm});
            skArc(sketch, "E11.27.3", {"start": v(43.45, 68.7) * mm, "mid": v(43.1, 68.81) * mm, "end": v(42.75, 68.75) * mm});
            skLineSegment(sketch, "E11.27.4", {"start": v(43.45, 68.7) * mm, "end": v(44.3, 68.22) * mm});
            skLineSegment(sketch, "E11.27.5", {"start": v(45.1, 67.64) * mm, "end": v(44.3, 68.22) * mm});
            skArc(sketch, "E11.27.6", {"start": v(45.42, 67.02) * mm, "mid": v(45.33, 67.37) * mm, "end": v(45.1, 67.64) * mm});
            skArc(sketch, "E11.27.7", {"start": v(44.79, 61.65) * mm, "mid": v(45.3, 64.31) * mm, "end": v(45.42, 67.02) * mm});
            skLineSegment(sketch, "E11.27.8", {"start": v(44.79, 61.65) * mm, "end": v(42.26, 58.17) * mm});
            skArc(sketch, "E11.27.9", {"start": v(42.26, 58.17) * mm, "mid": v(42.12, 57.59) * mm, "end": v(42.43, 57.08) * mm});
            skArc(sketch, "E11.28.0", {"start": v(21.24, 67.88) * mm, "mid": v(21.83, 67.93) * mm, "end": v(22.22, 68.38) * mm});
            skLineSegment(sketch, "E11.28.1", {"start": v(23.55, 72.47) * mm, "end": v(22.22, 68.38) * mm});
            skArc(sketch, "E11.28.2", {"start": v(23.55, 72.47) * mm, "mid": v(25.4, 74.45) * mm, "end": v(27.52, 76.14) * mm});
            skArc(sketch, "E11.28.3", {"start": v(28.21, 76.24) * mm, "mid": v(27.86, 76.27) * mm, "end": v(27.52, 76.14) * mm});
            skLineSegment(sketch, "E11.28.4", {"start": v(28.21, 76.24) * mm, "end": v(29.15, 75.94) * mm});
            skLineSegment(sketch, "E11.28.5", {"start": v(30.05, 75.54) * mm, "end": v(29.15, 75.94) * mm});
            skArc(sketch, "E11.28.6", {"start": v(30.5, 75) * mm, "mid": v(30.33, 75.32) * mm, "end": v(30.05, 75.54) * mm});
            skArc(sketch, "E11.28.7", {"start": v(31, 69.61) * mm, "mid": v(30.94, 72.32) * mm, "end": v(30.5, 75) * mm});
            skLineSegment(sketch, "E11.28.8", {"start": v(31, 69.61) * mm, "end": v(29.25, 65.69) * mm});
            skArc(sketch, "E11.28.9", {"start": v(29.25, 65.69) * mm, "mid": v(29.23, 65.09) * mm, "end": v(29.64, 64.65) * mm});
            skArc(sketch, "E11.29.0", {"start": v(6.66, 70.8) * mm, "mid": v(7.23, 70.98) * mm, "end": v(7.52, 71.5) * mm});
            skLineSegment(sketch, "E11.29.1", {"start": v(7.97, 75.78) * mm, "end": v(7.52, 71.5) * mm});
            skArc(sketch, "E11.29.2", {"start": v(7.97, 75.78) * mm, "mid": v(9.37, 78.1) * mm, "end": v(11.1, 80.2) * mm});
            skArc(sketch, "E11.29.3", {"start": v(11.75, 80.44) * mm, "mid": v(11.4, 80.4) * mm, "end": v(11.1, 80.2) * mm});
            skLineSegment(sketch, "E11.29.4", {"start": v(11.75, 80.44) * mm, "end": v(12.72, 80.34) * mm});
            skLineSegment(sketch, "E11.29.5", {"start": v(13.69, 80.13) * mm, "end": v(12.72, 80.34) * mm});
            skArc(sketch, "E11.29.6", {"start": v(14.23, 79.7) * mm, "mid": v(14.01, 79.98) * mm, "end": v(13.69, 80.13) * mm});
            skArc(sketch, "E11.29.7", {"start": v(15.84, 74.53) * mm, "mid": v(15.22, 77.18) * mm, "end": v(14.23, 79.7) * mm});
            skLineSegment(sketch, "E11.29.8", {"start": v(15.84, 74.53) * mm, "end": v(14.95, 70.33) * mm});
            skArc(sketch, "E11.29.9", {"start": v(14.95, 70.33) * mm, "mid": v(15.06, 69.74) * mm, "end": v(15.55, 69.4) * mm});
            skArc(sketch, "E12.trimOffspring", {"start": v(6.66, 70.8) * mm, "mid": v(3.72, 71.02) * mm, "end": v(0.78, 71.12) * mm});
            skArc(sketch, "E13.trimOffspring", {"start": v(21.24, 67.88) * mm, "mid": v(18.4, 68.7) * mm, "end": v(15.55, 69.4) * mm});
            skArc(sketch, "E14.trimOffspring", {"start": v(34.88, 61.98) * mm, "mid": v(32.29, 63.37) * mm, "end": v(29.64, 64.65) * mm});
            skArc(sketch, "E15.trimOffspring", {"start": v(47, 53.37) * mm, "mid": v(44.76, 55.27) * mm, "end": v(42.43, 57.08) * mm});
            skArc(sketch, "E16.trimOffspring", {"start": v(57.08, 42.43) * mm, "mid": v(55.27, 44.76) * mm, "end": v(53.37, 47) * mm});
            skArc(sketch, "E17.trimOffspring", {"start": v(64.65, 29.64) * mm, "mid": v(63.37, 32.29) * mm, "end": v(61.98, 34.88) * mm});
            skArc(sketch, "E18.trimOffspring", {"start": v(-22.72, 67.4) * mm, "mid": v(-25.49, 66.4) * mm, "end": v(-28.21, 65.28) * mm});
            skArc(sketch, "E19.trimOffspring", {"start": v(-36.23, 61.2) * mm, "mid": v(-38.73, 59.65) * mm, "end": v(-41.17, 58) * mm});
            skArc(sketch, "E20.trimOffspring", {"start": v(69.4, 15.55) * mm, "mid": v(68.7, 18.4) * mm, "end": v(67.88, 21.24) * mm});
            skArc(sketch, "E21.trimOffspring", {"start": v(71.12, 0.78) * mm, "mid": v(71.02, 3.72) * mm, "end": v(70.8, 6.66) * mm});
            skArc(sketch, "E22.trimOffspring", {"start": v(69.72, -14.02) * mm, "mid": v(70.24, -11.13) * mm, "end": v(70.64, -8.2) * mm});
            skArc(sketch, "E23.trimOffspring", {"start": v(65.28, -28.21) * mm, "mid": v(66.4, -25.49) * mm, "end": v(67.4, -22.72) * mm});
            skArc(sketch, "E24.trimOffspring", {"start": v(58, -41.17) * mm, "mid": v(59.65, -38.73) * mm, "end": v(61.2, -36.23) * mm});
            skArc(sketch, "E25.trimOffspring", {"start": v(48.16, -52.33) * mm, "mid": v(50.29, -50.29) * mm, "end": v(52.33, -48.16) * mm});
            skArc(sketch, "E26.trimOffspring", {"start": v(36.23, -61.2) * mm, "mid": v(38.73, -59.65) * mm, "end": v(41.17, -58) * mm});
            skArc(sketch, "E27.trimOffspring", {"start": v(22.72, -67.4) * mm, "mid": v(25.49, -66.4) * mm, "end": v(28.21, -65.28) * mm});
            skArc(sketch, "E28.trimOffspring", {"start": v(-6.66, -70.8) * mm, "mid": v(-3.72, -71.02) * mm, "end": v(-0.78, -71.12) * mm});
            skArc(sketch, "E29.trimOffspring", {"start": v(-21.24, -67.88) * mm, "mid": v(-18.4, -68.7) * mm, "end": v(-15.55, -69.4) * mm});
            skArc(sketch, "E30.trimOffspring", {"start": v(-57.08, -42.43) * mm, "mid": v(-55.27, -44.76) * mm, "end": v(-53.37, -47) * mm});
            skArc(sketch, "E31.trimOffspring", {"start": v(8.2, -70.64) * mm, "mid": v(11.13, -70.24) * mm, "end": v(14.02, -69.72) * mm});
            skArc(sketch, "E32.trimOffspring", {"start": v(-34.88, -61.98) * mm, "mid": v(-32.29, -63.37) * mm, "end": v(-29.64, -64.65) * mm});
            skArc(sketch, "E33.trimOffspring", {"start": v(-47, -53.37) * mm, "mid": v(-44.76, -55.27) * mm, "end": v(-42.43, -57.08) * mm});
            skArc(sketch, "E34.trimOffspring", {"start": v(-64.65, -29.64) * mm, "mid": v(-63.37, -32.29) * mm, "end": v(-61.98, -34.88) * mm});
            skArc(sketch, "E35.trimOffspring", {"start": v(-69.4, -15.55) * mm, "mid": v(-68.7, -18.4) * mm, "end": v(-67.88, -21.24) * mm});
            skArc(sketch, "E36.trimOffspring", {"start": v(-69.72, 14.02) * mm, "mid": v(-70.24, 11.13) * mm, "end": v(-70.64, 8.2) * mm});
            skArc(sketch, "E37.trimOffspring", {"start": v(-71.12, -0.78) * mm, "mid": v(-71.02, -3.72) * mm, "end": v(-70.8, -6.66) * mm});
            skArc(sketch, "E38.trimOffspring", {"start": v(-58, 41.17) * mm, "mid": v(-59.65, 38.73) * mm, "end": v(-61.2, 36.23) * mm});
            skArc(sketch, "E39.trimOffspring", {"start": v(-65.28, 28.21) * mm, "mid": v(-66.4, 25.49) * mm, "end": v(-67.4, 22.72) * mm});
            skArc(sketch, "E40.trimOffspring", {"start": v(-48.16, 52.33) * mm, "mid": v(-50.29, 50.29) * mm, "end": v(-52.33, 48.16) * mm});
            skArc(sketch, "E41", {"start": v(-4.93, 65.07) * mm, "mid": v(-6.22, 64.96) * mm, "end": v(-7.5, 64.82) * mm});
            skPoint(sketch, "E42.orphan", {"position": v(-3.8, 59.44) * mm});
            skPoint(sketch, "E43.orphan", {"position": v(0, 59.56) * mm});
            skArc(sketch, "E44.MirrorCS", {"start": v(-4, 62.56) * mm, "mid": v(-3.54, 61.48) * mm, "end": v(-3, 60.44) * mm});
            skLineSegment(sketch, "E45.MirrorCS", {"start": v(-2.32, 60.04) * mm, "end": v(-1.92, 60.04) * mm});
            skLineSegment(sketch, "E46.MirrorCS", {"start": v(-1.52, 60.06) * mm, "end": v(-1.92, 60.04) * mm});
            skArc(sketch, "E47.MirrorCS", {"start": v(0.01, 62.7) * mm, "mid": v(-0.38, 61.58) * mm, "end": v(-0.86, 60.5) * mm});
            skLineSegment(sketch, "E48.MirrorCS", {"start": v(0.01, 62.7) * mm, "end": v(-0.02, 64.44) * mm});
            skLineSegment(sketch, "E49.MirrorCS", {"start": v(-4, 62.56) * mm, "end": v(-4.08, 64.32) * mm});
            skPoint(sketch, "E50.visualSharp", {"position": v(-4.12, 65.12) * mm});
            skArc(sketch, "E50.filletArc", {"start": v(-4.08, 64.32) * mm, "mid": v(-4.35, 64.87) * mm, "end": v(-4.93, 65.07) * mm});
            skPoint(sketch, "E51.visualSharp", {"position": v(-0.04, 65.25) * mm});
            skArc(sketch, "E51.filletArc", {"start": v(0.77, 65.25) * mm, "mid": v(0.2, 65.01) * mm, "end": v(-0.02, 64.44) * mm});
            skPoint(sketch, "E52.visualSharp", {"position": v(-1.07, 60.09) * mm});
            skArc(sketch, "E52.filletArc", {"start": v(-1.52, 60.06) * mm, "mid": v(-1.13, 60.2) * mm, "end": v(-0.86, 60.5) * mm});
            skPoint(sketch, "E53.visualSharp", {"position": v(-2.77, 60.04) * mm});
            skArc(sketch, "E53.filletArc", {"start": v(-3, 60.44) * mm, "mid": v(-2.71, 60.14) * mm, "end": v(-2.32, 60.04) * mm});
            skArc(sketch, "E54.1.0", {"start": v(-12.21, 63.3) * mm, "mid": v(-12.54, 63.8) * mm, "end": v(-13.14, 63.93) * mm});
            skLineSegment(sketch, "E54.1.1", {"start": v(-11.91, 61.56) * mm, "end": v(-12.21, 63.3) * mm});
            skArc(sketch, "E54.1.2", {"start": v(-11.91, 61.56) * mm, "mid": v(-11.32, 60.55) * mm, "end": v(-10.65, 59.58) * mm});
            skArc(sketch, "E54.1.3", {"start": v(-10.65, 59.58) * mm, "mid": v(-10.33, 59.32) * mm, "end": v(-9.92, 59.27) * mm});
            skLineSegment(sketch, "E54.1.4", {"start": v(-9.92, 59.27) * mm, "end": v(-9.52, 59.32) * mm});
            skLineSegment(sketch, "E54.1.5", {"start": v(-9.13, 59.4) * mm, "end": v(-9.52, 59.32) * mm});
            skArc(sketch, "E54.1.6", {"start": v(-9.13, 59.4) * mm, "mid": v(-8.76, 59.57) * mm, "end": v(-8.53, 59.91) * mm});
            skArc(sketch, "E54.1.7", {"start": v(-7.95, 62.2) * mm, "mid": v(-8.2, 61.04) * mm, "end": v(-8.53, 59.91) * mm});
            skLineSegment(sketch, "E54.1.8", {"start": v(-7.95, 62.2) * mm, "end": v(-8.2, 63.93) * mm});
            skArc(sketch, "E54.1.9", {"start": v(-7.5, 64.82) * mm, "mid": v(-8.04, 64.52) * mm, "end": v(-8.2, 63.93) * mm});
            skArc(sketch, "E54.2.0", {"start": v(-20.15, 61.26) * mm, "mid": v(-20.54, 61.73) * mm, "end": v(-21.15, 61.77) * mm});
            skLineSegment(sketch, "E54.2.1", {"start": v(-19.64, 59.58) * mm, "end": v(-20.15, 61.26) * mm});
            skArc(sketch, "E54.2.2", {"start": v(-19.64, 59.58) * mm, "mid": v(-18.92, 58.64) * mm, "end": v(-18.13, 57.77) * mm});
            skArc(sketch, "E54.2.3", {"start": v(-18.13, 57.77) * mm, "mid": v(-17.78, 57.56) * mm, "end": v(-17.37, 57.55) * mm});
            skLineSegment(sketch, "E54.2.4", {"start": v(-17.37, 57.55) * mm, "end": v(-16.98, 57.65) * mm});
            skLineSegment(sketch, "E54.2.5", {"start": v(-16.6, 57.77) * mm, "end": v(-16.98, 57.65) * mm});
            skArc(sketch, "E54.2.6", {"start": v(-16.6, 57.77) * mm, "mid": v(-16.26, 58) * mm, "end": v(-16.07, 58.36) * mm});
            skArc(sketch, "E54.2.7", {"start": v(-15.78, 60.7) * mm, "mid": v(-15.88, 59.53) * mm, "end": v(-16.07, 58.36) * mm});
            skLineSegment(sketch, "E54.2.8", {"start": v(-15.78, 60.7) * mm, "end": v(-16.25, 62.4) * mm});
            skArc(sketch, "E54.2.9", {"start": v(-15.67, 63.37) * mm, "mid": v(-16.17, 63) * mm, "end": v(-16.25, 62.4) * mm});
            skArc(sketch, "E54.3.0", {"start": v(-27.76, 58.24) * mm, "mid": v(-28.21, 58.66) * mm, "end": v(-28.83, 58.63) * mm});
            skLineSegment(sketch, "E54.3.1", {"start": v(-27.05, 56.64) * mm, "end": v(-27.76, 58.24) * mm});
            skArc(sketch, "E54.3.2", {"start": v(-27.05, 56.64) * mm, "mid": v(-26.22, 55.8) * mm, "end": v(-25.33, 55.03) * mm});
            skArc(sketch, "E54.3.3", {"start": v(-25.33, 55.03) * mm, "mid": v(-24.95, 54.87) * mm, "end": v(-24.54, 54.91) * mm});
            skLineSegment(sketch, "E54.3.4", {"start": v(-24.54, 54.91) * mm, "end": v(-24.17, 55.06) * mm});
            skLineSegment(sketch, "E54.3.5", {"start": v(-23.81, 55.23) * mm, "end": v(-24.17, 55.06) * mm});
            skArc(sketch, "E54.3.6", {"start": v(-23.81, 55.23) * mm, "mid": v(-23.5, 55.5) * mm, "end": v(-23.36, 55.88) * mm});
            skArc(sketch, "E54.3.7", {"start": v(-23.36, 58.24) * mm, "mid": v(-23.32, 57.06) * mm, "end": v(-23.36, 55.88) * mm});
            skLineSegment(sketch, "E54.3.8", {"start": v(-23.36, 58.24) * mm, "end": v(-24.04, 59.86) * mm});
            skArc(sketch, "E54.3.9", {"start": v(-23.6, 60.9) * mm, "mid": v(-24.03, 60.47) * mm, "end": v(-24.04, 59.86) * mm});
            skArc(sketch, "E54.4.0", {"start": v(-34.94, 54.3) * mm, "mid": v(-35.44, 54.66) * mm, "end": v(-36.05, 54.55) * mm});
            skLineSegment(sketch, "E54.4.1", {"start": v(-34.03, 52.8) * mm, "end": v(-34.94, 54.3) * mm});
            skArc(sketch, "E54.4.2", {"start": v(-34.03, 52.8) * mm, "mid": v(-33.1, 52.07) * mm, "end": v(-32.12, 51.42) * mm});
            skArc(sketch, "E54.4.3", {"start": v(-32.12, 51.42) * mm, "mid": v(-31.73, 51.3) * mm, "end": v(-31.33, 51.4) * mm});
            skLineSegment(sketch, "E54.4.4", {"start": v(-31.33, 51.4) * mm, "end": v(-30.98, 51.6) * mm});
            skLineSegment(sketch, "E54.4.5", {"start": v(-30.65, 51.8) * mm, "end": v(-30.98, 51.6) * mm});
            skArc(sketch, "E54.4.6", {"start": v(-30.65, 51.8) * mm, "mid": v(-30.37, 52.1) * mm, "end": v(-30.28, 52.5) * mm});
            skArc(sketch, "E54.4.7", {"start": v(-30.57, 54.85) * mm, "mid": v(-30.38, 53.68) * mm, "end": v(-30.28, 52.5) * mm});
            skLineSegment(sketch, "E54.4.8", {"start": v(-30.57, 54.85) * mm, "end": v(-31.45, 56.37) * mm});
            skArc(sketch, "E54.4.9", {"start": v(-31.14, 57.45) * mm, "mid": v(-31.52, 56.98) * mm, "end": v(-31.45, 56.37) * mm});
            skArc(sketch, "E54.5.0", {"start": v(-41.57, 49.49) * mm, "mid": v(-42.11, 49.78) * mm, "end": v(-42.7, 49.6) * mm});
            skLineSegment(sketch, "E54.5.1", {"start": v(-40.48, 48.11) * mm, "end": v(-41.57, 49.49) * mm});
            skArc(sketch, "E54.5.2", {"start": v(-40.48, 48.11) * mm, "mid": v(-39.47, 47.5) * mm, "end": v(-38.41, 46.98) * mm});
            skArc(sketch, "E54.5.3", {"start": v(-38.41, 46.98) * mm, "mid": v(-38, 46.91) * mm, "end": v(-37.63, 47.06) * mm});
            skLineSegment(sketch, "E54.5.4", {"start": v(-37.63, 47.06) * mm, "end": v(-37.3, 47.3) * mm});
            skLineSegment(sketch, "E54.5.5", {"start": v(-37, 47.55) * mm, "end": v(-37.3, 47.3) * mm});
            skArc(sketch, "E54.5.6", {"start": v(-37, 47.55) * mm, "mid": v(-36.76, 47.89) * mm, "end": v(-36.72, 48.3) * mm});
            skArc(sketch, "E54.5.7", {"start": v(-37.3, 50.58) * mm, "mid": v(-36.97, 49.45) * mm, "end": v(-36.72, 48.3) * mm});
            skLineSegment(sketch, "E54.5.8", {"start": v(-37.3, 50.58) * mm, "end": v(-38.36, 51.98) * mm});
            skArc(sketch, "E54.5.9", {"start": v(-38.19, 53.1) * mm, "mid": v(-38.51, 52.57) * mm, "end": v(-38.36, 51.98) * mm});
            skArc(sketch, "E54.6.0", {"start": v(-47.55, 43.88) * mm, "mid": v(-48.12, 44.1) * mm, "end": v(-48.68, 43.85) * mm});
            skLineSegment(sketch, "E54.6.1", {"start": v(-46.29, 42.65) * mm, "end": v(-47.55, 43.88) * mm});
            skArc(sketch, "E54.6.2", {"start": v(-46.29, 42.65) * mm, "mid": v(-45.21, 42.18) * mm, "end": v(-44.1, 41.8) * mm});
            skArc(sketch, "E54.6.3", {"start": v(-44.1, 41.8) * mm, "mid": v(-43.69, 41.78) * mm, "end": v(-43.33, 41.97) * mm});
            skLineSegment(sketch, "E54.6.4", {"start": v(-43.33, 41.97) * mm, "end": v(-43.04, 42.24) * mm});
            skLineSegment(sketch, "E54.6.5", {"start": v(-42.76, 42.53) * mm, "end": v(-43.04, 42.24) * mm});
            skArc(sketch, "E54.6.6", {"start": v(-42.76, 42.53) * mm, "mid": v(-42.57, 42.9) * mm, "end": v(-42.58, 43.3) * mm});
            skArc(sketch, "E54.6.7", {"start": v(-43.45, 45.5) * mm, "mid": v(-42.98, 44.42) * mm, "end": v(-42.58, 43.3) * mm});
            skLineSegment(sketch, "E54.6.8", {"start": v(-43.45, 45.5) * mm, "end": v(-44.67, 46.75) * mm});
            skArc(sketch, "E54.6.9", {"start": v(-44.64, 47.88) * mm, "mid": v(-44.9, 47.32) * mm, "end": v(-44.67, 46.75) * mm});
            skArc(sketch, "E54.7.0", {"start": v(-52.77, 37.57) * mm, "mid": v(-53.36, 37.72) * mm, "end": v(-53.89, 37.4) * mm});
            skLineSegment(sketch, "E54.7.1", {"start": v(-51.37, 36.51) * mm, "end": v(-52.77, 37.57) * mm});
            skArc(sketch, "E54.7.2", {"start": v(-51.37, 36.51) * mm, "mid": v(-50.24, 36.18) * mm, "end": v(-49.09, 35.93) * mm});
            skArc(sketch, "E54.7.3", {"start": v(-49.09, 35.93) * mm, "mid": v(-48.68, 35.96) * mm, "end": v(-48.34, 36.2) * mm});
            skLineSegment(sketch, "E54.7.4", {"start": v(-48.34, 36.2) * mm, "end": v(-48.09, 36.5) * mm});
            skLineSegment(sketch, "E54.7.5", {"start": v(-47.85, 36.83) * mm, "end": v(-48.09, 36.5) * mm});
            skArc(sketch, "E54.7.6", {"start": v(-47.85, 36.83) * mm, "mid": v(-47.7, 37.22) * mm, "end": v(-47.77, 37.62) * mm});
            skArc(sketch, "E54.7.7", {"start": v(-48.9, 39.69) * mm, "mid": v(-48.3, 38.67) * mm, "end": v(-47.77, 37.62) * mm});
            skLineSegment(sketch, "E54.7.8", {"start": v(-48.9, 39.69) * mm, "end": v(-50.28, 40.78) * mm});
            skArc(sketch, "E54.7.9", {"start": v(-50.39, 41.9) * mm, "mid": v(-50.57, 41.32) * mm, "end": v(-50.28, 40.78) * mm});
            skArc(sketch, "E54.8.0", {"start": v(-57.16, 30.65) * mm, "mid": v(-57.77, 30.73) * mm, "end": v(-58.25, 30.34) * mm});
            skLineSegment(sketch, "E54.8.1", {"start": v(-55.64, 29.78) * mm, "end": v(-57.16, 30.65) * mm});
            skArc(sketch, "E54.8.2", {"start": v(-55.64, 29.78) * mm, "mid": v(-54.48, 29.6) * mm, "end": v(-53.3, 29.49) * mm});
            skArc(sketch, "E54.8.3", {"start": v(-53.3, 29.49) * mm, "mid": v(-52.9, 29.57) * mm, "end": v(-52.6, 29.85) * mm});
            skLineSegment(sketch, "E54.8.4", {"start": v(-52.6, 29.85) * mm, "end": v(-52.38, 30.19) * mm});
            skLineSegment(sketch, "E54.8.5", {"start": v(-52.2, 30.54) * mm, "end": v(-52.38, 30.19) * mm});
            skArc(sketch, "E54.8.6", {"start": v(-52.2, 30.54) * mm, "mid": v(-52.1, 30.94) * mm, "end": v(-52.21, 31.33) * mm});
            skArc(sketch, "E54.8.7", {"start": v(-53.6, 33.24) * mm, "mid": v(-52.87, 32.31) * mm, "end": v(-52.21, 31.33) * mm});
            skLineSegment(sketch, "E54.8.8", {"start": v(-53.6, 33.24) * mm, "end": v(-55.1, 34.15) * mm});
            skArc(sketch, "E54.8.9", {"start": v(-55.34, 35.25) * mm, "mid": v(-55.45, 34.65) * mm, "end": v(-55.1, 34.15) * mm});
            skArc(sketch, "E54.9.0", {"start": v(-60.65, 23.24) * mm, "mid": v(-61.26, 23.24) * mm, "end": v(-61.69, 22.8) * mm});
            skLineSegment(sketch, "E54.9.1", {"start": v(-59.03, 22.57) * mm, "end": v(-60.65, 23.24) * mm});
            skArc(sketch, "E54.9.2", {"start": v(-59.03, 22.57) * mm, "mid": v(-57.85, 22.52) * mm, "end": v(-56.68, 22.57) * mm});
            skArc(sketch, "E54.9.3", {"start": v(-56.68, 22.57) * mm, "mid": v(-56.29, 22.7) * mm, "end": v(-56.02, 23.02) * mm});
            skLineSegment(sketch, "E54.9.4", {"start": v(-56.02, 23.02) * mm, "end": v(-55.85, 23.38) * mm});
            skLineSegment(sketch, "E54.9.5", {"start": v(-55.7, 23.75) * mm, "end": v(-55.85, 23.38) * mm});
            skArc(sketch, "E54.9.6", {"start": v(-55.7, 23.75) * mm, "mid": v(-55.66, 24.16) * mm, "end": v(-55.83, 24.53) * mm});
            skArc(sketch, "E54.9.7", {"start": v(-57.44, 26.25) * mm, "mid": v(-56.6, 25.42) * mm, "end": v(-55.83, 24.53) * mm});
            skLineSegment(sketch, "E54.9.8", {"start": v(-57.44, 26.25) * mm, "end": v(-59.04, 26.97) * mm});
            skArc(sketch, "E54.9.9", {"start": v(-59.42, 28.03) * mm, "mid": v(-59.46, 27.42) * mm, "end": v(-59.04, 26.97) * mm});
            skArc(sketch, "E54.10.0", {"start": v(-63.18, 15.45) * mm, "mid": v(-63.8, 15.37) * mm, "end": v(-64.16, 14.88) * mm});
            skLineSegment(sketch, "E54.10.1", {"start": v(-61.5, 14.98) * mm, "end": v(-63.18, 15.45) * mm});
            skArc(sketch, "E54.10.2", {"start": v(-61.5, 14.98) * mm, "mid": v(-60.32, 15.09) * mm, "end": v(-59.16, 15.28) * mm});
            skArc(sketch, "E54.10.3", {"start": v(-59.16, 15.28) * mm, "mid": v(-58.8, 15.47) * mm, "end": v(-58.57, 15.8) * mm});
            skLineSegment(sketch, "E54.10.4", {"start": v(-58.57, 15.8) * mm, "end": v(-58.44, 16.19) * mm});
            skLineSegment(sketch, "E54.10.5", {"start": v(-58.34, 16.58) * mm, "end": v(-58.44, 16.19) * mm});
            skArc(sketch, "E54.10.6", {"start": v(-58.34, 16.58) * mm, "mid": v(-58.35, 16.99) * mm, "end": v(-58.56, 17.34) * mm});
            skArc(sketch, "E54.10.7", {"start": v(-60.37, 18.84) * mm, "mid": v(-59.44, 18.12) * mm, "end": v(-58.56, 17.34) * mm});
            skLineSegment(sketch, "E54.10.8", {"start": v(-60.37, 18.84) * mm, "end": v(-62.05, 19.35) * mm});
            skArc(sketch, "E54.10.9", {"start": v(-62.57, 20.36) * mm, "mid": v(-62.52, 19.75) * mm, "end": v(-62.05, 19.35) * mm});
            skArc(sketch, "E54.11.0", {"start": v(-64.72, 7.4) * mm, "mid": v(-65.31, 7.25) * mm, "end": v(-65.62, 6.72) * mm});
            skLineSegment(sketch, "E54.11.1", {"start": v(-62.99, 7.15) * mm, "end": v(-64.72, 7.4) * mm});
            skArc(sketch, "E54.11.2", {"start": v(-62.99, 7.15) * mm, "mid": v(-61.83, 7.4) * mm, "end": v(-60.7, 7.74) * mm});
            skArc(sketch, "E54.11.3", {"start": v(-60.7, 7.74) * mm, "mid": v(-60.36, 7.97) * mm, "end": v(-60.18, 8.34) * mm});
            skLineSegment(sketch, "E54.11.4", {"start": v(-60.18, 8.34) * mm, "end": v(-60.1, 8.73) * mm});
            skLineSegment(sketch, "E54.11.5", {"start": v(-60.06, 9.13) * mm, "end": v(-60.1, 8.73) * mm});
            skArc(sketch, "E54.11.6", {"start": v(-60.06, 9.13) * mm, "mid": v(-60.12, 9.53) * mm, "end": v(-60.37, 9.86) * mm});
            skArc(sketch, "E54.11.7", {"start": v(-62.36, 11.12) * mm, "mid": v(-61.34, 10.53) * mm, "end": v(-60.37, 9.86) * mm});
            skLineSegment(sketch, "E54.11.8", {"start": v(-62.36, 11.12) * mm, "end": v(-64.09, 11.42) * mm});
            skArc(sketch, "E54.11.9", {"start": v(-64.72, 12.35) * mm, "mid": v(-64.6, 11.75) * mm, "end": v(-64.09, 11.42) * mm});
            skArc(sketch, "E54.12.0", {"start": v(-65.24, -0.77) * mm, "mid": v(-65.8, -1) * mm, "end": v(-66.04, -1.57) * mm});
            skLineSegment(sketch, "E54.12.1", {"start": v(-63.48, -0.8) * mm, "end": v(-65.24, -0.77) * mm});
            skArc(sketch, "E54.12.2", {"start": v(-63.48, -0.8) * mm, "mid": v(-62.37, -0.4) * mm, "end": v(-61.3, 0.07) * mm});
            skArc(sketch, "E54.12.3", {"start": v(-61.3, 0.07) * mm, "mid": v(-60.99, 0.34) * mm, "end": v(-60.85, 0.72) * mm});
            skLineSegment(sketch, "E54.12.4", {"start": v(-60.85, 0.72) * mm, "end": v(-60.83, 1.12) * mm});
            skLineSegment(sketch, "E54.12.5", {"start": v(-60.83, 1.52) * mm, "end": v(-60.83, 1.12) * mm});
            skArc(sketch, "E54.12.6", {"start": v(-60.83, 1.52) * mm, "mid": v(-60.94, 1.92) * mm, "end": v(-61.23, 2.2) * mm});
            skArc(sketch, "E54.12.7", {"start": v(-63.36, 3.21) * mm, "mid": v(-62.27, 2.75) * mm, "end": v(-61.23, 2.2) * mm});
            skLineSegment(sketch, "E54.12.8", {"start": v(-63.36, 3.21) * mm, "end": v(-65.11, 3.29) * mm});
            skArc(sketch, "E54.12.9", {"start": v(-65.86, 4.13) * mm, "mid": v(-65.66, 3.55) * mm, "end": v(-65.11, 3.29) * mm});
            skArc(sketch, "E54.13.0", {"start": v(-64.73, -8.95) * mm, "mid": v(-65.26, -9.24) * mm, "end": v(-65.42, -9.84) * mm});
            skLineSegment(sketch, "E54.13.1", {"start": v(-62.98, -8.76) * mm, "end": v(-64.73, -8.95) * mm});
            skArc(sketch, "E54.13.2", {"start": v(-62.98, -8.76) * mm, "mid": v(-61.93, -8.23) * mm, "end": v(-60.92, -7.62) * mm});
            skArc(sketch, "E54.13.3", {"start": v(-60.92, -7.62) * mm, "mid": v(-60.65, -7.32) * mm, "end": v(-60.56, -6.91) * mm});
            skLineSegment(sketch, "E54.13.4", {"start": v(-60.56, -6.91) * mm, "end": v(-60.59, -6.52) * mm});
            skLineSegment(sketch, "E54.13.5", {"start": v(-60.64, -6.12) * mm, "end": v(-60.59, -6.52) * mm});
            skArc(sketch, "E54.13.6", {"start": v(-60.64, -6.12) * mm, "mid": v(-60.8, -5.74) * mm, "end": v(-61.12, -5.5) * mm});
            skArc(sketch, "E54.13.7", {"start": v(-63.36, -4.76) * mm, "mid": v(-62.23, -5.08) * mm, "end": v(-61.12, -5.5) * mm});
            skLineSegment(sketch, "E54.13.8", {"start": v(-63.36, -4.76) * mm, "end": v(-65.1, -4.9) * mm});
            skArc(sketch, "E54.13.9", {"start": v(-65.96, -4.16) * mm, "mid": v(-65.7, -4.71) * mm, "end": v(-65.1, -4.9) * mm});
            skArc(sketch, "E54.14.0", {"start": v(-63.2, -17) * mm, "mid": v(-63.69, -17.36) * mm, "end": v(-63.77, -17.96) * mm});
            skLineSegment(sketch, "E54.14.1", {"start": v(-61.49, -16.59) * mm, "end": v(-63.2, -17) * mm});
            skArc(sketch, "E54.14.2", {"start": v(-61.49, -16.59) * mm, "mid": v(-60.5, -15.93) * mm, "end": v(-59.58, -15.2) * mm});
            skArc(sketch, "E54.14.3", {"start": v(-59.58, -15.2) * mm, "mid": v(-59.35, -14.87) * mm, "end": v(-59.32, -14.46) * mm});
            skLineSegment(sketch, "E54.14.4", {"start": v(-59.32, -14.46) * mm, "end": v(-59.4, -14.06) * mm});
            skLineSegment(sketch, "E54.14.5", {"start": v(-59.5, -13.68) * mm, "end": v(-59.4, -14.06) * mm});
            skArc(sketch, "E54.14.6", {"start": v(-59.5, -13.68) * mm, "mid": v(-59.7, -13.32) * mm, "end": v(-60.05, -13.11) * mm});
            skArc(sketch, "E54.14.7", {"start": v(-62.36, -12.67) * mm, "mid": v(-61.2, -12.85) * mm, "end": v(-60.05, -13.11) * mm});
            skLineSegment(sketch, "E54.14.8", {"start": v(-62.36, -12.67) * mm, "end": v(-64.08, -13.03) * mm});
            skArc(sketch, "E54.14.9", {"start": v(-65.02, -12.4) * mm, "mid": v(-64.68, -12.91) * mm, "end": v(-64.08, -13.03) * mm});
            skArc(sketch, "E54.15.0", {"start": v(-60.66, -24.79) * mm, "mid": v(-61.1, -25.2) * mm, "end": v(-61.12, -25.82) * mm});
            skLineSegment(sketch, "E54.15.1", {"start": v(-59.02, -24.17) * mm, "end": v(-60.66, -24.79) * mm});
            skArc(sketch, "E54.15.2", {"start": v(-59.02, -24.17) * mm, "mid": v(-58.13, -23.4) * mm, "end": v(-57.3, -22.56) * mm});
            skArc(sketch, "E54.15.3", {"start": v(-57.3, -22.56) * mm, "mid": v(-57.12, -22.2) * mm, "end": v(-57.14, -21.78) * mm});
            skLineSegment(sketch, "E54.15.4", {"start": v(-57.14, -21.78) * mm, "end": v(-57.26, -21.4) * mm});
            skLineSegment(sketch, "E54.15.5", {"start": v(-57.4, -21.03) * mm, "end": v(-57.26, -21.4) * mm});
            skArc(sketch, "E54.15.6", {"start": v(-57.4, -21.03) * mm, "mid": v(-57.65, -20.7) * mm, "end": v(-58.03, -20.54) * mm});
            skArc(sketch, "E54.15.7", {"start": v(-60.38, -20.4) * mm, "mid": v(-59.2, -20.42) * mm, "end": v(-58.03, -20.54) * mm});
            skLineSegment(sketch, "E54.15.8", {"start": v(-60.38, -20.4) * mm, "end": v(-62.04, -20.96) * mm});
            skArc(sketch, "E54.15.9", {"start": v(-63.05, -20.45) * mm, "mid": v(-62.65, -20.92) * mm, "end": v(-62.04, -20.96) * mm});
            skArc(sketch, "E54.16.0", {"start": v(-57.18, -32.2) * mm, "mid": v(-57.57, -32.67) * mm, "end": v(-57.5, -33.28) * mm});
            skLineSegment(sketch, "E54.16.1", {"start": v(-55.62, -31.38) * mm, "end": v(-57.18, -32.2) * mm});
            skArc(sketch, "E54.16.2", {"start": v(-55.62, -31.38) * mm, "mid": v(-54.84, -30.5) * mm, "end": v(-54.13, -29.57) * mm});
            skArc(sketch, "E54.16.3", {"start": v(-54.13, -29.57) * mm, "mid": v(-53.98, -29.18) * mm, "end": v(-54.06, -28.78) * mm});
            skLineSegment(sketch, "E54.16.4", {"start": v(-54.06, -28.78) * mm, "end": v(-54.23, -28.42) * mm});
            skLineSegment(sketch, "E54.16.5", {"start": v(-54.42, -28.07) * mm, "end": v(-54.23, -28.42) * mm});
            skArc(sketch, "E54.16.6", {"start": v(-54.42, -28.07) * mm, "mid": v(-54.7, -27.77) * mm, "end": v(-55.1, -27.66) * mm});
            skArc(sketch, "E54.16.7", {"start": v(-57.45, -27.8) * mm, "mid": v(-56.28, -27.69) * mm, "end": v(-55.1, -27.66) * mm});
            skLineSegment(sketch, "E54.16.8", {"start": v(-57.45, -27.8) * mm, "end": v(-59.02, -28.58) * mm});
            skArc(sketch, "E54.16.9", {"start": v(-60.09, -28.2) * mm, "mid": v(-59.63, -28.62) * mm, "end": v(-59.02, -28.58) * mm});
            skArc(sketch, "E54.17.0", {"start": v(-52.8, -39.12) * mm, "mid": v(-53.12, -39.64) * mm, "end": v(-52.97, -40.23) * mm});
            skLineSegment(sketch, "E54.17.1", {"start": v(-51.35, -38.11) * mm, "end": v(-52.8, -39.12) * mm});
            skArc(sketch, "E54.17.2", {"start": v(-51.35, -38.11) * mm, "mid": v(-50.69, -37.14) * mm, "end": v(-50.1, -36.12) * mm});
            skArc(sketch, "E54.17.3", {"start": v(-50.1, -36.12) * mm, "mid": v(-50, -35.72) * mm, "end": v(-50.12, -35.33) * mm});
            skLineSegment(sketch, "E54.17.4", {"start": v(-50.12, -35.33) * mm, "end": v(-50.34, -35) * mm});
            skLineSegment(sketch, "E54.17.5", {"start": v(-50.57, -34.67) * mm, "end": v(-50.34, -35) * mm});
            skArc(sketch, "E54.17.6", {"start": v(-50.57, -34.67) * mm, "mid": v(-50.9, -34.41) * mm, "end": v(-51.3, -34.35) * mm});
            skArc(sketch, "E54.17.7", {"start": v(-53.61, -34.79) * mm, "mid": v(-52.46, -34.53) * mm, "end": v(-51.3, -34.35) * mm});
            skLineSegment(sketch, "E54.17.8", {"start": v(-53.61, -34.79) * mm, "end": v(-55.07, -35.76) * mm});
            skArc(sketch, "E54.17.9", {"start": v(-56.18, -35.52) * mm, "mid": v(-55.68, -35.87) * mm, "end": v(-55.07, -35.76) * mm});
            skArc(sketch, "E54.18.0", {"start": v(-47.57, -45.43) * mm, "mid": v(-47.83, -45.99) * mm, "end": v(-47.6, -46.56) * mm});
            skLineSegment(sketch, "E54.18.1", {"start": v(-46.27, -44.25) * mm, "end": v(-47.57, -45.43) * mm});
            skArc(sketch, "E54.18.2", {"start": v(-46.27, -44.25) * mm, "mid": v(-45.73, -43.2) * mm, "end": v(-45.27, -42.12) * mm});
            skArc(sketch, "E54.18.3", {"start": v(-45.27, -42.12) * mm, "mid": v(-45.23, -41.71) * mm, "end": v(-45.4, -41.34) * mm});
            skLineSegment(sketch, "E54.18.4", {"start": v(-45.4, -41.34) * mm, "end": v(-45.65, -41.03) * mm});
            skLineSegment(sketch, "E54.18.5", {"start": v(-45.93, -40.74) * mm, "end": v(-45.65, -41.03) * mm});
            skArc(sketch, "E54.18.6", {"start": v(-45.93, -40.74) * mm, "mid": v(-46.27, -40.53) * mm, "end": v(-46.69, -40.52) * mm});
            skArc(sketch, "E54.18.7", {"start": v(-48.93, -41.24) * mm, "mid": v(-47.82, -40.84) * mm, "end": v(-46.69, -40.52) * mm});
            skLineSegment(sketch, "E54.18.8", {"start": v(-48.93, -41.24) * mm, "end": v(-50.26, -42.38) * mm});
            skArc(sketch, "E54.18.9", {"start": v(-51.38, -42.28) * mm, "mid": v(-50.84, -42.57) * mm, "end": v(-50.26, -42.38) * mm});
            skArc(sketch, "E54.19.0", {"start": v(-41.6, -51.04) * mm, "mid": v(-41.79, -51.62) * mm, "end": v(-41.5, -52.17) * mm});
            skLineSegment(sketch, "E54.19.1", {"start": v(-40.46, -49.7) * mm, "end": v(-41.6, -51.04) * mm});
            skArc(sketch, "E54.19.2", {"start": v(-40.46, -49.7) * mm, "mid": v(-40.05, -48.6) * mm, "end": v(-39.73, -47.47) * mm});
            skArc(sketch, "E54.19.3", {"start": v(-39.73, -47.47) * mm, "mid": v(-39.74, -47.06) * mm, "end": v(-39.96, -46.7) * mm});
            skLineSegment(sketch, "E54.19.4", {"start": v(-39.96, -46.7) * mm, "end": v(-40.25, -46.44) * mm});
            skLineSegment(sketch, "E54.19.5", {"start": v(-40.56, -46.18) * mm, "end": v(-40.25, -46.44) * mm});
            skArc(sketch, "E54.19.6", {"start": v(-40.56, -46.18) * mm, "mid": v(-40.93, -46.01) * mm, "end": v(-41.34, -46.05) * mm});
            skArc(sketch, "E54.19.7", {"start": v(-43.47, -47.05) * mm, "mid": v(-42.42, -46.51) * mm, "end": v(-41.34, -46.05) * mm});
            skLineSegment(sketch, "E54.19.8", {"start": v(-43.47, -47.05) * mm, "end": v(-44.65, -48.35) * mm});
            skArc(sketch, "E54.19.9", {"start": v(-45.78, -48.4) * mm, "mid": v(-45.2, -48.61) * mm, "end": v(-44.65, -48.35) * mm});
            skArc(sketch, "E54.20.0", {"start": v(-34.97, -55.86) * mm, "mid": v(-35.09, -56.46) * mm, "end": v(-34.73, -56.96) * mm});
            skLineSegment(sketch, "E54.20.1", {"start": v(-34, -54.4) * mm, "end": v(-34.97, -55.86) * mm});
            skArc(sketch, "E54.20.2", {"start": v(-34, -54.4) * mm, "mid": v(-33.74, -53.25) * mm, "end": v(-33.57, -52.08) * mm});
            skArc(sketch, "E54.20.3", {"start": v(-33.57, -52.08) * mm, "mid": v(-33.63, -51.67) * mm, "end": v(-33.89, -51.35) * mm});
            skLineSegment(sketch, "E54.20.4", {"start": v(-33.89, -51.35) * mm, "end": v(-34.2, -51.12) * mm});
            skLineSegment(sketch, "E54.20.5", {"start": v(-34.55, -50.9) * mm, "end": v(-34.2, -51.12) * mm});
            skArc(sketch, "E54.20.6", {"start": v(-34.55, -50.9) * mm, "mid": v(-34.94, -50.78) * mm, "end": v(-35.34, -50.88) * mm});
            skArc(sketch, "E54.20.7", {"start": v(-37.33, -52.14) * mm, "mid": v(-36.36, -51.47) * mm, "end": v(-35.34, -50.88) * mm});
            skLineSegment(sketch, "E54.20.8", {"start": v(-37.33, -52.14) * mm, "end": v(-38.33, -53.57) * mm});
            skArc(sketch, "E54.20.9", {"start": v(-39.45, -53.75) * mm, "mid": v(-38.85, -53.9) * mm, "end": v(-38.33, -53.57) * mm});
            skArc(sketch, "E54.21.0", {"start": v(-27.8, -59.8) * mm, "mid": v(-27.83, -60.42) * mm, "end": v(-27.42, -60.87) * mm});
            skLineSegment(sketch, "E54.21.1", {"start": v(-27.02, -58.23) * mm, "end": v(-27.8, -59.8) * mm});
            skArc(sketch, "E54.21.2", {"start": v(-27.02, -58.23) * mm, "mid": v(-26.9, -57.06) * mm, "end": v(-26.87, -55.88) * mm});
            skArc(sketch, "E54.21.3", {"start": v(-26.87, -55.88) * mm, "mid": v(-26.99, -55.49) * mm, "end": v(-27.28, -55.2) * mm});
            skLineSegment(sketch, "E54.21.4", {"start": v(-27.28, -55.2) * mm, "end": v(-27.63, -55.01) * mm});
            skLineSegment(sketch, "E54.21.5", {"start": v(-28, -54.84) * mm, "end": v(-27.63, -55.01) * mm});
            skArc(sketch, "E54.21.6", {"start": v(-28, -54.84) * mm, "mid": v(-28.4, -54.77) * mm, "end": v(-28.78, -54.91) * mm});
            skArc(sketch, "E54.21.7", {"start": v(-30.6, -56.4) * mm, "mid": v(-29.72, -55.63) * mm, "end": v(-28.78, -54.91) * mm});
            skLineSegment(sketch, "E54.21.8", {"start": v(-30.6, -56.4) * mm, "end": v(-31.41, -57.96) * mm});
            skArc(sketch, "E54.21.9", {"start": v(-32.5, -58.28) * mm, "mid": v(-31.89, -58.35) * mm, "end": v(-31.41, -57.96) * mm});
            skArc(sketch, "E54.22.0", {"start": v(-20.18, -62.82) * mm, "mid": v(-20.14, -63.44) * mm, "end": v(-19.67, -63.83) * mm});
            skLineSegment(sketch, "E54.22.1", {"start": v(-19.6, -61.17) * mm, "end": v(-20.18, -62.82) * mm});
            skArc(sketch, "E54.22.2", {"start": v(-19.6, -61.17) * mm, "mid": v(-19.64, -59.99) * mm, "end": v(-19.76, -58.82) * mm});
            skArc(sketch, "E54.22.3", {"start": v(-19.76, -58.82) * mm, "mid": v(-19.92, -58.44) * mm, "end": v(-20.25, -58.2) * mm});
            skLineSegment(sketch, "E54.22.4", {"start": v(-20.25, -58.2) * mm, "end": v(-20.62, -58.05) * mm});
            skLineSegment(sketch, "E54.22.5", {"start": v(-21, -57.92) * mm, "end": v(-20.62, -58.05) * mm});
            skArc(sketch, "E54.22.6", {"start": v(-21, -57.92) * mm, "mid": v(-21.4, -57.9) * mm, "end": v(-21.77, -58.1) * mm});
            skArc(sketch, "E54.22.7", {"start": v(-23.39, -59.8) * mm, "mid": v(-22.61, -58.92) * mm, "end": v(-21.77, -58.1) * mm});
            skLineSegment(sketch, "E54.22.8", {"start": v(-23.39, -59.8) * mm, "end": v(-24, -61.45) * mm});
            skArc(sketch, "E54.22.9", {"start": v(-25.04, -61.9) * mm, "mid": v(-24.42, -61.9) * mm, "end": v(-24, -61.45) * mm});
            skArc(sketch, "E54.23.0", {"start": v(-12.25, -64.86) * mm, "mid": v(-12.13, -65.47) * mm, "end": v(-11.61, -65.8) * mm});
            skLineSegment(sketch, "E54.23.1", {"start": v(-11.88, -63.15) * mm, "end": v(-12.25, -64.86) * mm});
            skArc(sketch, "E54.23.2", {"start": v(-11.88, -63.15) * mm, "mid": v(-12.06, -61.98) * mm, "end": v(-12.33, -60.83) * mm});
            skArc(sketch, "E54.23.3", {"start": v(-12.33, -60.83) * mm, "mid": v(-12.54, -60.48) * mm, "end": v(-12.9, -60.28) * mm});
            skLineSegment(sketch, "E54.23.4", {"start": v(-12.9, -60.28) * mm, "end": v(-13.28, -60.18) * mm});
            skLineSegment(sketch, "E54.23.5", {"start": v(-13.67, -60.1) * mm, "end": v(-13.28, -60.18) * mm});
            skArc(sketch, "E54.23.6", {"start": v(-13.67, -60.1) * mm, "mid": v(-14.08, -60.13) * mm, "end": v(-14.42, -60.37) * mm});
            skArc(sketch, "E54.23.7", {"start": v(-15.8, -62.27) * mm, "mid": v(-15.15, -61.3) * mm, "end": v(-14.42, -60.37) * mm});
            skLineSegment(sketch, "E54.23.8", {"start": v(-15.8, -62.27) * mm, "end": v(-16.2, -63.98) * mm});
            skArc(sketch, "E54.23.9", {"start": v(-17.18, -64.56) * mm, "mid": v(-16.57, -64.47) * mm, "end": v(-16.2, -63.98) * mm});
            skArc(sketch, "E54.24.0", {"start": v(-4.12, -65.9) * mm, "mid": v(-3.93, -66.47) * mm, "end": v(-3.37, -66.74) * mm});
            skLineSegment(sketch, "E54.24.1", {"start": v(-3.98, -64.14) * mm, "end": v(-4.12, -65.9) * mm});
            skArc(sketch, "E54.24.2", {"start": v(-3.98, -64.14) * mm, "mid": v(-4.3, -63.01) * mm, "end": v(-4.7, -61.9) * mm});
            skArc(sketch, "E54.24.3", {"start": v(-4.7, -61.9) * mm, "mid": v(-4.96, -61.58) * mm, "end": v(-5.34, -61.42) * mm});
            skLineSegment(sketch, "E54.24.4", {"start": v(-5.34, -61.42) * mm, "end": v(-5.73, -61.37) * mm});
            skLineSegment(sketch, "E54.24.5", {"start": v(-6.13, -61.35) * mm, "end": v(-5.73, -61.37) * mm});
            skArc(sketch, "E54.24.6", {"start": v(-6.13, -61.35) * mm, "mid": v(-6.53, -61.43) * mm, "end": v(-6.84, -61.7) * mm});
            skArc(sketch, "E54.24.7", {"start": v(-7.98, -63.77) * mm, "mid": v(-7.45, -62.71) * mm, "end": v(-6.84, -61.7) * mm});
            skLineSegment(sketch, "E54.24.8", {"start": v(-7.98, -63.77) * mm, "end": v(-8.16, -65.5) * mm});
            skArc(sketch, "E54.24.9", {"start": v(-9.05, -66.2) * mm, "mid": v(-8.46, -66.05) * mm, "end": v(-8.16, -65.5) * mm});
            skArc(sketch, "E54.25.0", {"start": v(4.07, -65.9) * mm, "mid": v(4.34, -66.45) * mm, "end": v(4.92, -66.64) * mm});
            skLineSegment(sketch, "E54.25.1", {"start": v(4, -64.14) * mm, "end": v(4.07, -65.9) * mm});
            skArc(sketch, "E54.25.2", {"start": v(4, -64.14) * mm, "mid": v(3.53, -63.06) * mm, "end": v(3, -62.01) * mm});
            skArc(sketch, "E54.25.3", {"start": v(3, -62.01) * mm, "mid": v(2.7, -61.72) * mm, "end": v(2.3, -61.61) * mm});
            skLineSegment(sketch, "E54.25.4", {"start": v(2.3, -61.61) * mm, "end": v(1.9, -61.61) * mm});
            skLineSegment(sketch, "E54.25.5", {"start": v(1.5, -61.64) * mm, "end": v(1.9, -61.61) * mm});
            skArc(sketch, "E54.25.6", {"start": v(1.5, -61.64) * mm, "mid": v(1.12, -61.77) * mm, "end": v(0.85, -62.08) * mm});
            skArc(sketch, "E54.25.7", {"start": v(-0.02, -64.27) * mm, "mid": v(0.37, -63.16) * mm, "end": v(0.85, -62.08) * mm});
            skLineSegment(sketch, "E54.25.8", {"start": v(-0.02, -64.27) * mm, "end": v(0.01, -66.02) * mm});
            skArc(sketch, "E54.25.9", {"start": v(-0.78, -66.82) * mm, "mid": v(-0.21, -66.6) * mm, "end": v(0.01, -66.02) * mm});
            skArc(sketch, "E54.26.0", {"start": v(12.2, -64.87) * mm, "mid": v(12.53, -65.39) * mm, "end": v(13.13, -65.5) * mm});
            skLineSegment(sketch, "E54.26.1", {"start": v(11.9, -63.14) * mm, "end": v(12.2, -64.87) * mm});
            skArc(sketch, "E54.26.2", {"start": v(11.9, -63.14) * mm, "mid": v(11.3, -62.12) * mm, "end": v(10.64, -61.15) * mm});
            skArc(sketch, "E54.26.3", {"start": v(10.64, -61.15) * mm, "mid": v(10.32, -60.9) * mm, "end": v(9.91, -60.84) * mm});
            skLineSegment(sketch, "E54.26.4", {"start": v(9.91, -60.84) * mm, "end": v(9.52, -60.9) * mm});
            skLineSegment(sketch, "E54.26.5", {"start": v(9.12, -60.97) * mm, "end": v(9.52, -60.9) * mm});
            skArc(sketch, "E54.26.6", {"start": v(9.12, -60.97) * mm, "mid": v(8.75, -61.15) * mm, "end": v(8.52, -61.49) * mm});
            skArc(sketch, "E54.26.7", {"start": v(7.94, -63.77) * mm, "mid": v(8.19, -62.62) * mm, "end": v(8.52, -61.49) * mm});
            skLineSegment(sketch, "E54.26.8", {"start": v(7.94, -63.77) * mm, "end": v(8.19, -65.5) * mm});
            skArc(sketch, "E54.26.9", {"start": v(7.5, -66.4) * mm, "mid": v(8.03, -66.1) * mm, "end": v(8.19, -65.5) * mm});
            skArc(sketch, "E54.27.0", {"start": v(20.14, -62.83) * mm, "mid": v(20.53, -63.3) * mm, "end": v(21.14, -63.35) * mm});
            skLineSegment(sketch, "E54.27.1", {"start": v(19.63, -61.16) * mm, "end": v(20.14, -62.83) * mm});
            skArc(sketch, "E54.27.2", {"start": v(19.63, -61.16) * mm, "mid": v(18.9, -60.22) * mm, "end": v(18.12, -59.34) * mm});
            skArc(sketch, "E54.27.3", {"start": v(18.12, -59.34) * mm, "mid": v(17.77, -59.13) * mm, "end": v(17.36, -59.13) * mm});
            skLineSegment(sketch, "E54.27.4", {"start": v(17.36, -59.13) * mm, "end": v(16.97, -59.23) * mm});
            skLineSegment(sketch, "E54.27.5", {"start": v(16.6, -59.35) * mm, "end": v(16.97, -59.23) * mm});
            skArc(sketch, "E54.27.6", {"start": v(16.6, -59.35) * mm, "mid": v(16.25, -59.57) * mm, "end": v(16.07, -59.94) * mm});
            skArc(sketch, "E54.27.7", {"start": v(15.77, -62.28) * mm, "mid": v(15.87, -61.1) * mm, "end": v(16.07, -59.94) * mm});
            skLineSegment(sketch, "E54.27.8", {"start": v(15.77, -62.28) * mm, "end": v(16.24, -63.97) * mm});
            skArc(sketch, "E54.27.9", {"start": v(15.66, -64.94) * mm, "mid": v(16.16, -64.58) * mm, "end": v(16.24, -63.97) * mm});
            skArc(sketch, "E54.28.0", {"start": v(27.75, -59.82) * mm, "mid": v(28.2, -60.24) * mm, "end": v(28.82, -60.2) * mm});
            skLineSegment(sketch, "E54.28.1", {"start": v(27.04, -58.22) * mm, "end": v(27.75, -59.82) * mm});
            skArc(sketch, "E54.28.2", {"start": v(27.04, -58.22) * mm, "mid": v(26.2, -57.38) * mm, "end": v(25.32, -56.61) * mm});
            skArc(sketch, "E54.28.3", {"start": v(25.32, -56.61) * mm, "mid": v(24.94, -56.44) * mm, "end": v(24.53, -56.5) * mm});
            skLineSegment(sketch, "E54.28.4", {"start": v(24.53, -56.5) * mm, "end": v(24.16, -56.64) * mm});
            skLineSegment(sketch, "E54.28.5", {"start": v(23.8, -56.8) * mm, "end": v(24.16, -56.64) * mm});
            skArc(sketch, "E54.28.6", {"start": v(23.8, -56.8) * mm, "mid": v(23.49, -57.07) * mm, "end": v(23.35, -57.46) * mm});
            skArc(sketch, "E54.28.7", {"start": v(23.35, -59.82) * mm, "mid": v(23.3, -58.64) * mm, "end": v(23.35, -57.46) * mm});
            skLineSegment(sketch, "E54.28.8", {"start": v(23.35, -59.82) * mm, "end": v(24.03, -61.43) * mm});
            skArc(sketch, "E54.28.9", {"start": v(23.58, -62.47) * mm, "mid": v(24.02, -62.05) * mm, "end": v(24.03, -61.43) * mm});
            skArc(sketch, "E54.29.0", {"start": v(34.93, -55.88) * mm, "mid": v(35.43, -56.24) * mm, "end": v(36.04, -56.13) * mm});
            skLineSegment(sketch, "E54.29.1", {"start": v(34.02, -54.38) * mm, "end": v(34.93, -55.88) * mm});
            skArc(sketch, "E54.29.2", {"start": v(34.02, -54.38) * mm, "mid": v(33.1, -53.65) * mm, "end": v(32.12, -53) * mm});
            skArc(sketch, "E54.29.3", {"start": v(32.12, -53) * mm, "mid": v(31.72, -52.88) * mm, "end": v(31.32, -52.98) * mm});
            skLineSegment(sketch, "E54.29.4", {"start": v(31.32, -52.98) * mm, "end": v(30.97, -53.17) * mm});
            skLineSegment(sketch, "E54.29.5", {"start": v(30.64, -53.38) * mm, "end": v(30.97, -53.17) * mm});
            skArc(sketch, "E54.29.6", {"start": v(30.64, -53.38) * mm, "mid": v(30.36, -53.69) * mm, "end": v(30.27, -54.09) * mm});
            skArc(sketch, "E54.29.7", {"start": v(30.56, -56.42) * mm, "mid": v(30.37, -55.26) * mm, "end": v(30.27, -54.09) * mm});
            skLineSegment(sketch, "E54.29.8", {"start": v(30.56, -56.42) * mm, "end": v(31.44, -57.94) * mm});
            skArc(sketch, "E54.29.9", {"start": v(31.13, -59.03) * mm, "mid": v(31.51, -58.55) * mm, "end": v(31.44, -57.94) * mm});
            skArc(sketch, "E54.30.0", {"start": v(41.56, -51.06) * mm, "mid": v(42.1, -51.36) * mm, "end": v(42.69, -51.17) * mm});
            skLineSegment(sketch, "E54.30.1", {"start": v(40.47, -49.7) * mm, "end": v(41.56, -51.06) * mm});
            skArc(sketch, "E54.30.2", {"start": v(40.47, -49.7) * mm, "mid": v(39.46, -49.09) * mm, "end": v(38.4, -48.56) * mm});
            skArc(sketch, "E54.30.3", {"start": v(38.4, -48.56) * mm, "mid": v(38, -48.5) * mm, "end": v(37.62, -48.64) * mm});
            skLineSegment(sketch, "E54.30.4", {"start": v(37.62, -48.64) * mm, "end": v(37.3, -48.87) * mm});
            skLineSegment(sketch, "E54.30.5", {"start": v(36.99, -49.13) * mm, "end": v(37.3, -48.87) * mm});
            skArc(sketch, "E54.30.6", {"start": v(36.99, -49.13) * mm, "mid": v(36.75, -49.46) * mm, "end": v(36.71, -49.87) * mm});
            skArc(sketch, "E54.30.7", {"start": v(37.3, -52.15) * mm, "mid": v(36.96, -51.02) * mm, "end": v(36.71, -49.87) * mm});
            skLineSegment(sketch, "E54.30.8", {"start": v(37.3, -52.15) * mm, "end": v(38.35, -53.55) * mm});
            skArc(sketch, "E54.30.9", {"start": v(38.18, -54.67) * mm, "mid": v(38.5, -54.15) * mm, "end": v(38.35, -53.55) * mm});
            skArc(sketch, "E54.31.0", {"start": v(47.54, -45.46) * mm, "mid": v(48.1, -45.68) * mm, "end": v(48.67, -45.43) * mm});
            skLineSegment(sketch, "E54.31.1", {"start": v(46.28, -44.23) * mm, "end": v(47.54, -45.46) * mm});
            skArc(sketch, "E54.31.2", {"start": v(46.28, -44.23) * mm, "mid": v(45.2, -43.76) * mm, "end": v(44.09, -43.37) * mm});
            skArc(sketch, "E54.31.3", {"start": v(44.09, -43.37) * mm, "mid": v(43.68, -43.35) * mm, "end": v(43.32, -43.55) * mm});
            skLineSegment(sketch, "E54.31.4", {"start": v(43.32, -43.55) * mm, "end": v(43.03, -43.82) * mm});
            skLineSegment(sketch, "E54.31.5", {"start": v(42.75, -44.11) * mm, "end": v(43.03, -43.82) * mm});
            skArc(sketch, "E54.31.6", {"start": v(42.75, -44.11) * mm, "mid": v(42.56, -44.47) * mm, "end": v(42.57, -44.88) * mm});
            skArc(sketch, "E54.31.7", {"start": v(43.44, -47.07) * mm, "mid": v(42.97, -46) * mm, "end": v(42.57, -44.88) * mm});
            skLineSegment(sketch, "E54.31.8", {"start": v(43.44, -47.07) * mm, "end": v(44.66, -48.33) * mm});
            skArc(sketch, "E54.31.9", {"start": v(44.63, -49.46) * mm, "mid": v(44.89, -48.9) * mm, "end": v(44.66, -48.33) * mm});
            skArc(sketch, "E54.32.0", {"start": v(52.76, -39.15) * mm, "mid": v(53.35, -39.3) * mm, "end": v(53.88, -38.97) * mm});
            skLineSegment(sketch, "E54.32.1", {"start": v(51.36, -38.09) * mm, "end": v(52.76, -39.15) * mm});
            skArc(sketch, "E54.32.2", {"start": v(51.36, -38.09) * mm, "mid": v(50.23, -37.75) * mm, "end": v(49.08, -37.5) * mm});
            skArc(sketch, "E54.32.3", {"start": v(49.08, -37.5) * mm, "mid": v(48.67, -37.54) * mm, "end": v(48.33, -37.78) * mm});
            skLineSegment(sketch, "E54.32.4", {"start": v(48.33, -37.78) * mm, "end": v(48.08, -38.09) * mm});
            skLineSegment(sketch, "E54.32.5", {"start": v(47.85, -38.4) * mm, "end": v(48.08, -38.09) * mm});
            skArc(sketch, "E54.32.6", {"start": v(47.85, -38.4) * mm, "mid": v(47.7, -38.8) * mm, "end": v(47.77, -39.2) * mm});
            skArc(sketch, "E54.32.7", {"start": v(48.9, -41.26) * mm, "mid": v(48.3, -40.25) * mm, "end": v(47.77, -39.2) * mm});
            skLineSegment(sketch, "E54.32.8", {"start": v(48.9, -41.26) * mm, "end": v(50.27, -42.36) * mm});
            skArc(sketch, "E54.32.9", {"start": v(50.38, -43.48) * mm, "mid": v(50.56, -42.9) * mm, "end": v(50.27, -42.36) * mm});
            skArc(sketch, "E54.33.0", {"start": v(57.15, -32.23) * mm, "mid": v(57.76, -32.3) * mm, "end": v(58.24, -31.92) * mm});
            skLineSegment(sketch, "E54.33.1", {"start": v(55.63, -31.36) * mm, "end": v(57.15, -32.23) * mm});
            skArc(sketch, "E54.33.2", {"start": v(55.63, -31.36) * mm, "mid": v(54.47, -31.17) * mm, "end": v(53.3, -31.06) * mm});
            skArc(sketch, "E54.33.3", {"start": v(53.3, -31.06) * mm, "mid": v(52.9, -31.15) * mm, "end": v(52.59, -31.43) * mm});
            skLineSegment(sketch, "E54.33.4", {"start": v(52.59, -31.43) * mm, "end": v(52.38, -31.77) * mm});
            skLineSegment(sketch, "E54.33.5", {"start": v(52.18, -32.12) * mm, "end": v(52.38, -31.77) * mm});
            skArc(sketch, "E54.33.6", {"start": v(52.18, -32.12) * mm, "mid": v(52.09, -32.51) * mm, "end": v(52.2, -32.9) * mm});
            skArc(sketch, "E54.33.7", {"start": v(53.58, -34.82) * mm, "mid": v(52.86, -33.89) * mm, "end": v(52.2, -32.9) * mm});
            skLineSegment(sketch, "E54.33.8", {"start": v(53.58, -34.82) * mm, "end": v(55.08, -35.73) * mm});
            skArc(sketch, "E54.33.9", {"start": v(55.33, -36.83) * mm, "mid": v(55.44, -36.23) * mm, "end": v(55.08, -35.73) * mm});
            skArc(sketch, "E54.34.0", {"start": v(60.64, -24.82) * mm, "mid": v(61.25, -24.82) * mm, "end": v(61.68, -24.37) * mm});
            skLineSegment(sketch, "E54.34.1", {"start": v(59.02, -24.14) * mm, "end": v(60.64, -24.82) * mm});
            skArc(sketch, "E54.34.2", {"start": v(59.02, -24.14) * mm, "mid": v(57.84, -24.1) * mm, "end": v(56.67, -24.15) * mm});
            skArc(sketch, "E54.34.3", {"start": v(56.67, -24.15) * mm, "mid": v(56.28, -24.28) * mm, "end": v(56.01, -24.6) * mm});
            skLineSegment(sketch, "E54.34.4", {"start": v(56.01, -24.6) * mm, "end": v(55.84, -24.96) * mm});
            skLineSegment(sketch, "E54.34.5", {"start": v(55.7, -25.33) * mm, "end": v(55.84, -24.96) * mm});
            skArc(sketch, "E54.34.6", {"start": v(55.7, -25.33) * mm, "mid": v(55.65, -25.74) * mm, "end": v(55.82, -26.11) * mm});
            skArc(sketch, "E54.34.7", {"start": v(57.43, -27.83) * mm, "mid": v(56.59, -27) * mm, "end": v(55.82, -26.11) * mm});
            skLineSegment(sketch, "E54.34.8", {"start": v(57.43, -27.83) * mm, "end": v(59.03, -28.55) * mm});
            skArc(sketch, "E54.34.9", {"start": v(59.41, -29.6) * mm, "mid": v(59.45, -29) * mm, "end": v(59.03, -28.55) * mm});
            skArc(sketch, "E54.35.0", {"start": v(63.17, -17.03) * mm, "mid": v(63.78, -16.95) * mm, "end": v(64.15, -16.46) * mm});
            skLineSegment(sketch, "E54.35.1", {"start": v(61.48, -16.56) * mm, "end": v(63.17, -17.03) * mm});
            skArc(sketch, "E54.35.2", {"start": v(61.48, -16.56) * mm, "mid": v(60.31, -16.67) * mm, "end": v(59.15, -16.86) * mm});
            skArc(sketch, "E54.35.3", {"start": v(59.15, -16.86) * mm, "mid": v(58.78, -17.04) * mm, "end": v(58.56, -17.39) * mm});
            skLineSegment(sketch, "E54.35.4", {"start": v(58.56, -17.39) * mm, "end": v(58.43, -17.77) * mm});
            skLineSegment(sketch, "E54.35.5", {"start": v(58.33, -18.15) * mm, "end": v(58.43, -17.77) * mm});
            skArc(sketch, "E54.35.6", {"start": v(58.33, -18.15) * mm, "mid": v(58.34, -18.56) * mm, "end": v(58.55, -18.92) * mm});
            skArc(sketch, "E54.35.7", {"start": v(60.36, -20.42) * mm, "mid": v(59.43, -19.7) * mm, "end": v(58.55, -18.92) * mm});
            skLineSegment(sketch, "E54.35.8", {"start": v(60.36, -20.42) * mm, "end": v(62.04, -20.93) * mm});
            skArc(sketch, "E54.35.9", {"start": v(62.56, -21.93) * mm, "mid": v(62.51, -21.32) * mm, "end": v(62.04, -20.93) * mm});
            skArc(sketch, "E54.36.0", {"start": v(64.71, -8.98) * mm, "mid": v(65.3, -8.83) * mm, "end": v(65.6, -8.3) * mm});
            skLineSegment(sketch, "E54.36.1", {"start": v(62.98, -8.73) * mm, "end": v(64.71, -8.98) * mm});
            skArc(sketch, "E54.36.2", {"start": v(62.98, -8.73) * mm, "mid": v(61.83, -8.98) * mm, "end": v(60.7, -9.32) * mm});
            skArc(sketch, "E54.36.3", {"start": v(60.7, -9.32) * mm, "mid": v(60.35, -9.55) * mm, "end": v(60.18, -9.92) * mm});
            skLineSegment(sketch, "E54.36.4", {"start": v(60.18, -9.92) * mm, "end": v(60.1, -10.3) * mm});
            skLineSegment(sketch, "E54.36.5", {"start": v(60.05, -10.7) * mm, "end": v(60.1, -10.3) * mm});
            skArc(sketch, "E54.36.6", {"start": v(60.05, -10.7) * mm, "mid": v(60.1, -11.11) * mm, "end": v(60.36, -11.43) * mm});
            skArc(sketch, "E54.36.7", {"start": v(62.35, -12.7) * mm, "mid": v(61.33, -12.1) * mm, "end": v(60.36, -11.43) * mm});
            skLineSegment(sketch, "E54.36.8", {"start": v(62.35, -12.7) * mm, "end": v(64.08, -13) * mm});
            skArc(sketch, "E54.36.9", {"start": v(64.72, -13.93) * mm, "mid": v(64.6, -13.33) * mm, "end": v(64.08, -13) * mm});
            skArc(sketch, "E54.37.0", {"start": v(65.23, -0.8) * mm, "mid": v(65.8, -0.58) * mm, "end": v(66.03, -0.01) * mm});
            skLineSegment(sketch, "E54.37.1", {"start": v(63.47, -0.77) * mm, "end": v(65.23, -0.8) * mm});
            skArc(sketch, "E54.37.2", {"start": v(63.47, -0.77) * mm, "mid": v(62.36, -1.17) * mm, "end": v(61.29, -1.64) * mm});
            skArc(sketch, "E54.37.3", {"start": v(61.29, -1.64) * mm, "mid": v(60.98, -1.91) * mm, "end": v(60.84, -2.3) * mm});
            skLineSegment(sketch, "E54.37.4", {"start": v(60.84, -2.3) * mm, "end": v(60.82, -2.7) * mm});
            skLineSegment(sketch, "E54.37.5", {"start": v(60.82, -3.1) * mm, "end": v(60.82, -2.7) * mm});
            skArc(sketch, "E54.37.6", {"start": v(60.82, -3.1) * mm, "mid": v(60.93, -3.5) * mm, "end": v(61.22, -3.78) * mm});
            skArc(sketch, "E54.37.7", {"start": v(63.35, -4.79) * mm, "mid": v(62.27, -4.33) * mm, "end": v(61.22, -3.78) * mm});
            skLineSegment(sketch, "E54.37.8", {"start": v(63.35, -4.79) * mm, "end": v(65.1, -4.87) * mm});
            skArc(sketch, "E54.37.9", {"start": v(65.85, -5.71) * mm, "mid": v(65.66, -5.13) * mm, "end": v(65.1, -4.87) * mm});
            skArc(sketch, "E54.38.0", {"start": v(64.72, 7.37) * mm, "mid": v(65.25, 7.67) * mm, "end": v(65.41, 8.26) * mm});
            skLineSegment(sketch, "E54.38.1", {"start": v(62.97, 7.18) * mm, "end": v(64.72, 7.37) * mm});
            skArc(sketch, "E54.38.2", {"start": v(62.97, 7.18) * mm, "mid": v(61.92, 6.65) * mm, "end": v(60.91, 6.05) * mm});
            skArc(sketch, "E54.38.3", {"start": v(60.91, 6.05) * mm, "mid": v(60.64, 5.74) * mm, "end": v(60.55, 5.34) * mm});
            skLineSegment(sketch, "E54.38.4", {"start": v(60.55, 5.34) * mm, "end": v(60.58, 4.94) * mm});
            skLineSegment(sketch, "E54.38.5", {"start": v(60.63, 4.54) * mm, "end": v(60.58, 4.94) * mm});
            skArc(sketch, "E54.38.6", {"start": v(60.63, 4.54) * mm, "mid": v(60.79, 4.16) * mm, "end": v(61.11, 3.91) * mm});
            skArc(sketch, "E54.38.7", {"start": v(63.35, 3.18) * mm, "mid": v(62.22, 3.5) * mm, "end": v(61.11, 3.91) * mm});
            skLineSegment(sketch, "E54.38.8", {"start": v(63.35, 3.18) * mm, "end": v(65.1, 3.33) * mm});
            skArc(sketch, "E54.38.9", {"start": v(65.95, 2.58) * mm, "mid": v(65.68, 3.13) * mm, "end": v(65.1, 3.33) * mm});
            skArc(sketch, "E54.39.0", {"start": v(63.18, 15.42) * mm, "mid": v(63.68, 15.78) * mm, "end": v(63.76, 16.39) * mm});
            skLineSegment(sketch, "E54.39.1", {"start": v(61.48, 15.01) * mm, "end": v(63.18, 15.42) * mm});
            skArc(sketch, "E54.39.2", {"start": v(61.48, 15.01) * mm, "mid": v(60.5, 14.35) * mm, "end": v(59.57, 13.63) * mm});
            skArc(sketch, "E54.39.3", {"start": v(59.57, 13.63) * mm, "mid": v(59.34, 13.29) * mm, "end": v(59.3, 12.88) * mm});
            skLineSegment(sketch, "E54.39.4", {"start": v(59.3, 12.88) * mm, "end": v(59.38, 12.49) * mm});
            skLineSegment(sketch, "E54.39.5", {"start": v(59.48, 12.1) * mm, "end": v(59.38, 12.49) * mm});
            skArc(sketch, "E54.39.6", {"start": v(59.48, 12.1) * mm, "mid": v(59.69, 11.74) * mm, "end": v(60.04, 11.54) * mm});
            skArc(sketch, "E54.39.7", {"start": v(62.35, 11.1) * mm, "mid": v(61.19, 11.27) * mm, "end": v(60.04, 11.54) * mm});
            skLineSegment(sketch, "E54.39.8", {"start": v(62.35, 11.1) * mm, "end": v(64.07, 11.45) * mm});
            skArc(sketch, "E54.39.9", {"start": v(65, 10.82) * mm, "mid": v(64.67, 11.34) * mm, "end": v(64.07, 11.45) * mm});
            skArc(sketch, "E54.40.0", {"start": v(60.65, 23.2) * mm, "mid": v(61.1, 23.63) * mm, "end": v(61.1, 24.24) * mm});
            skLineSegment(sketch, "E54.40.1", {"start": v(59.01, 22.6) * mm, "end": v(60.65, 23.2) * mm});
            skArc(sketch, "E54.40.2", {"start": v(59.01, 22.6) * mm, "mid": v(58.12, 21.82) * mm, "end": v(57.3, 20.98) * mm});
            skArc(sketch, "E54.40.3", {"start": v(57.3, 20.98) * mm, "mid": v(57.1, 20.61) * mm, "end": v(57.13, 20.2) * mm});
            skLineSegment(sketch, "E54.40.4", {"start": v(57.13, 20.2) * mm, "end": v(57.25, 19.83) * mm});
            skLineSegment(sketch, "E54.40.5", {"start": v(57.4, 19.45) * mm, "end": v(57.25, 19.83) * mm});
            skArc(sketch, "E54.40.6", {"start": v(57.4, 19.45) * mm, "mid": v(57.64, 19.12) * mm, "end": v(58.02, 18.96) * mm});
            skArc(sketch, "E54.40.7", {"start": v(60.37, 18.81) * mm, "mid": v(59.2, 18.84) * mm, "end": v(58.02, 18.96) * mm});
            skLineSegment(sketch, "E54.40.8", {"start": v(60.37, 18.81) * mm, "end": v(62.03, 19.39) * mm});
            skArc(sketch, "E54.40.9", {"start": v(63.04, 18.88) * mm, "mid": v(62.64, 19.35) * mm, "end": v(62.03, 19.39) * mm});
            skArc(sketch, "E54.41.0", {"start": v(57.17, 30.62) * mm, "mid": v(57.56, 31.1) * mm, "end": v(57.49, 31.7) * mm});
            skLineSegment(sketch, "E54.41.1", {"start": v(55.62, 29.8) * mm, "end": v(57.17, 30.62) * mm});
            skArc(sketch, "E54.41.2", {"start": v(55.62, 29.8) * mm, "mid": v(54.83, 28.93) * mm, "end": v(54.12, 27.99) * mm});
            skArc(sketch, "E54.41.3", {"start": v(54.12, 27.99) * mm, "mid": v(53.98, 27.6) * mm, "end": v(54.05, 27.2) * mm});
            skLineSegment(sketch, "E54.41.4", {"start": v(54.05, 27.2) * mm, "end": v(54.22, 26.84) * mm});
            skLineSegment(sketch, "E54.41.5", {"start": v(54.4, 26.49) * mm, "end": v(54.22, 26.84) * mm});
            skArc(sketch, "E54.41.6", {"start": v(54.4, 26.49) * mm, "mid": v(54.7, 26.2) * mm, "end": v(55.09, 26.08) * mm});
            skArc(sketch, "E54.41.7", {"start": v(57.44, 26.23) * mm, "mid": v(56.27, 26.1) * mm, "end": v(55.09, 26.08) * mm});
            skLineSegment(sketch, "E54.41.8", {"start": v(57.44, 26.23) * mm, "end": v(59.01, 27) * mm});
            skArc(sketch, "E54.41.9", {"start": v(60.08, 26.62) * mm, "mid": v(59.62, 27.04) * mm, "end": v(59.01, 27) * mm});
            skArc(sketch, "E54.42.0", {"start": v(52.78, 37.54) * mm, "mid": v(53.1, 38.06) * mm, "end": v(52.96, 38.66) * mm});
            skLineSegment(sketch, "E54.42.1", {"start": v(51.34, 36.54) * mm, "end": v(52.78, 37.54) * mm});
            skArc(sketch, "E54.42.2", {"start": v(51.34, 36.54) * mm, "mid": v(50.68, 35.56) * mm, "end": v(50.08, 34.55) * mm});
            skArc(sketch, "E54.42.3", {"start": v(50.08, 34.55) * mm, "mid": v(50, 34.15) * mm, "end": v(50.11, 33.75) * mm});
            skLineSegment(sketch, "E54.42.4", {"start": v(50.11, 33.75) * mm, "end": v(50.33, 33.42) * mm});
            skLineSegment(sketch, "E54.42.5", {"start": v(50.56, 33.1) * mm, "end": v(50.33, 33.42) * mm});
            skArc(sketch, "E54.42.6", {"start": v(50.56, 33.1) * mm, "mid": v(50.88, 32.84) * mm, "end": v(51.29, 32.77) * mm});
            skArc(sketch, "E54.42.7", {"start": v(53.6, 33.21) * mm, "mid": v(52.45, 32.95) * mm, "end": v(51.29, 32.77) * mm});
            skLineSegment(sketch, "E54.42.8", {"start": v(53.6, 33.21) * mm, "end": v(55.06, 34.18) * mm});
            skArc(sketch, "E54.42.9", {"start": v(56.17, 33.94) * mm, "mid": v(55.67, 34.3) * mm, "end": v(55.06, 34.18) * mm});
            skArc(sketch, "E54.43.0", {"start": v(47.56, 43.85) * mm, "mid": v(47.82, 44.4) * mm, "end": v(47.6, 44.98) * mm});
            skLineSegment(sketch, "E54.43.1", {"start": v(46.26, 42.68) * mm, "end": v(47.56, 43.85) * mm});
            skArc(sketch, "E54.43.2", {"start": v(46.26, 42.68) * mm, "mid": v(45.72, 41.63) * mm, "end": v(45.26, 40.54) * mm});
            skArc(sketch, "E54.43.3", {"start": v(45.26, 40.54) * mm, "mid": v(45.22, 40.14) * mm, "end": v(45.39, 39.76) * mm});
            skLineSegment(sketch, "E54.43.4", {"start": v(45.39, 39.76) * mm, "end": v(45.64, 39.46) * mm});
            skLineSegment(sketch, "E54.43.5", {"start": v(45.92, 39.16) * mm, "end": v(45.64, 39.46) * mm});
            skArc(sketch, "E54.43.6", {"start": v(45.92, 39.16) * mm, "mid": v(46.27, 38.95) * mm, "end": v(46.68, 38.94) * mm});
            skArc(sketch, "E54.43.7", {"start": v(48.92, 39.66) * mm, "mid": v(47.8, 39.26) * mm, "end": v(46.68, 38.94) * mm});
            skLineSegment(sketch, "E54.43.8", {"start": v(48.92, 39.66) * mm, "end": v(50.25, 40.8) * mm});
            skArc(sketch, "E54.43.9", {"start": v(51.37, 40.7) * mm, "mid": v(50.83, 41) * mm, "end": v(50.25, 40.8) * mm});
            skArc(sketch, "E54.44.0", {"start": v(41.6, 49.46) * mm, "mid": v(41.78, 50.05) * mm, "end": v(41.49, 50.59) * mm});
            skLineSegment(sketch, "E54.44.1", {"start": v(40.45, 48.13) * mm, "end": v(41.6, 49.46) * mm});
            skArc(sketch, "E54.44.2", {"start": v(40.45, 48.13) * mm, "mid": v(40.04, 47.03) * mm, "end": v(39.72, 45.9) * mm});
            skArc(sketch, "E54.44.3", {"start": v(39.72, 45.9) * mm, "mid": v(39.73, 45.48) * mm, "end": v(39.95, 45.13) * mm});
            skLineSegment(sketch, "E54.44.4", {"start": v(39.95, 45.13) * mm, "end": v(40.24, 44.86) * mm});
            skLineSegment(sketch, "E54.44.5", {"start": v(40.55, 44.6) * mm, "end": v(40.24, 44.86) * mm});
            skArc(sketch, "E54.44.6", {"start": v(40.55, 44.6) * mm, "mid": v(40.92, 44.43) * mm, "end": v(41.33, 44.48) * mm});
            skArc(sketch, "E54.44.7", {"start": v(43.46, 45.48) * mm, "mid": v(42.41, 44.94) * mm, "end": v(41.33, 44.48) * mm});
            skLineSegment(sketch, "E54.44.8", {"start": v(43.46, 45.48) * mm, "end": v(44.64, 46.78) * mm});
            skArc(sketch, "E54.44.9", {"start": v(45.77, 46.82) * mm, "mid": v(45.2, 47.04) * mm, "end": v(44.64, 46.78) * mm});
            skArc(sketch, "E54.45.0", {"start": v(34.96, 54.28) * mm, "mid": v(35.08, 54.88) * mm, "end": v(34.72, 55.38) * mm});
            skLineSegment(sketch, "E54.45.1", {"start": v(34, 52.82) * mm, "end": v(34.96, 54.28) * mm});
            skArc(sketch, "E54.45.2", {"start": v(34, 52.82) * mm, "mid": v(33.73, 51.67) * mm, "end": v(33.56, 50.5) * mm});
            skArc(sketch, "E54.45.3", {"start": v(33.56, 50.5) * mm, "mid": v(33.62, 50.1) * mm, "end": v(33.88, 49.78) * mm});
            skLineSegment(sketch, "E54.45.4", {"start": v(33.88, 49.78) * mm, "end": v(34.2, 49.54) * mm});
            skLineSegment(sketch, "E54.45.5", {"start": v(34.54, 49.33) * mm, "end": v(34.2, 49.54) * mm});
            skArc(sketch, "E54.45.6", {"start": v(34.54, 49.33) * mm, "mid": v(34.93, 49.2) * mm, "end": v(35.33, 49.3) * mm});
            skArc(sketch, "E54.45.7", {"start": v(37.32, 50.56) * mm, "mid": v(36.35, 49.9) * mm, "end": v(35.33, 49.3) * mm});
            skLineSegment(sketch, "E54.45.8", {"start": v(37.32, 50.56) * mm, "end": v(38.32, 52) * mm});
            skArc(sketch, "E54.45.9", {"start": v(39.44, 52.18) * mm, "mid": v(38.84, 52.32) * mm, "end": v(38.32, 52) * mm});
            skArc(sketch, "E54.46.0", {"start": v(27.79, 58.23) * mm, "mid": v(27.82, 58.84) * mm, "end": v(27.4, 59.3) * mm});
            skLineSegment(sketch, "E54.46.1", {"start": v(27, 56.66) * mm, "end": v(27.79, 58.23) * mm});
            skArc(sketch, "E54.46.2", {"start": v(27, 56.66) * mm, "mid": v(26.9, 55.48) * mm, "end": v(26.87, 54.3) * mm});
            skArc(sketch, "E54.46.3", {"start": v(26.87, 54.3) * mm, "mid": v(26.98, 53.91) * mm, "end": v(27.27, 53.63) * mm});
            skLineSegment(sketch, "E54.46.4", {"start": v(27.27, 53.63) * mm, "end": v(27.62, 53.43) * mm});
            skLineSegment(sketch, "E54.46.5", {"start": v(27.98, 53.26) * mm, "end": v(27.62, 53.43) * mm});
            skArc(sketch, "E54.46.6", {"start": v(27.98, 53.26) * mm, "mid": v(28.39, 53.2) * mm, "end": v(28.77, 53.33) * mm});
            skArc(sketch, "E54.46.7", {"start": v(30.59, 54.83) * mm, "mid": v(29.7, 54.05) * mm, "end": v(28.77, 53.33) * mm});
            skLineSegment(sketch, "E54.46.8", {"start": v(30.59, 54.83) * mm, "end": v(31.4, 56.38) * mm});
            skArc(sketch, "E54.46.9", {"start": v(32.5, 56.7) * mm, "mid": v(31.88, 56.77) * mm, "end": v(31.4, 56.38) * mm});
            skArc(sketch, "E54.47.0", {"start": v(20.17, 61.25) * mm, "mid": v(20.13, 61.86) * mm, "end": v(19.66, 62.26) * mm});
            skLineSegment(sketch, "E54.47.1", {"start": v(19.6, 59.59) * mm, "end": v(20.17, 61.25) * mm});
            skArc(sketch, "E54.47.2", {"start": v(19.6, 59.59) * mm, "mid": v(19.63, 58.41) * mm, "end": v(19.75, 57.24) * mm});
            skArc(sketch, "E54.47.3", {"start": v(19.75, 57.24) * mm, "mid": v(19.9, 56.86) * mm, "end": v(20.24, 56.62) * mm});
            skLineSegment(sketch, "E54.47.4", {"start": v(20.24, 56.62) * mm, "end": v(20.6, 56.47) * mm});
            skLineSegment(sketch, "E54.47.5", {"start": v(20.99, 56.34) * mm, "end": v(20.6, 56.47) * mm});
            skArc(sketch, "E54.47.6", {"start": v(20.99, 56.34) * mm, "mid": v(21.4, 56.32) * mm, "end": v(21.76, 56.51) * mm});
            skArc(sketch, "E54.47.7", {"start": v(23.38, 58.23) * mm, "mid": v(22.6, 57.34) * mm, "end": v(21.76, 56.51) * mm});
            skLineSegment(sketch, "E54.47.8", {"start": v(23.38, 58.23) * mm, "end": v(24, 59.87) * mm});
            skArc(sketch, "E54.47.9", {"start": v(25.03, 60.32) * mm, "mid": v(24.41, 60.32) * mm, "end": v(24, 59.87) * mm});
            skArc(sketch, "E54.48.0", {"start": v(12.24, 63.29) * mm, "mid": v(12.12, 63.89) * mm, "end": v(11.6, 64.22) * mm});
            skLineSegment(sketch, "E54.48.1", {"start": v(11.88, 61.57) * mm, "end": v(12.24, 63.29) * mm});
            skArc(sketch, "E54.48.2", {"start": v(11.88, 61.57) * mm, "mid": v(12.05, 60.4) * mm, "end": v(12.32, 59.26) * mm});
            skArc(sketch, "E54.48.3", {"start": v(12.32, 59.26) * mm, "mid": v(12.53, 58.9) * mm, "end": v(12.88, 58.7) * mm});
            skLineSegment(sketch, "E54.48.4", {"start": v(12.88, 58.7) * mm, "end": v(13.27, 58.6) * mm});
            skLineSegment(sketch, "E54.48.5", {"start": v(13.66, 58.53) * mm, "end": v(13.27, 58.6) * mm});
            skArc(sketch, "E54.48.6", {"start": v(13.66, 58.53) * mm, "mid": v(14.07, 58.56) * mm, "end": v(14.41, 58.79) * mm});
            skArc(sketch, "E54.48.7", {"start": v(15.8, 60.7) * mm, "mid": v(15.14, 59.72) * mm, "end": v(14.41, 58.79) * mm});
            skLineSegment(sketch, "E54.48.8", {"start": v(15.8, 60.7) * mm, "end": v(16.2, 62.4) * mm});
            skArc(sketch, "E54.48.9", {"start": v(17.17, 62.98) * mm, "mid": v(16.56, 62.9) * mm, "end": v(16.2, 62.4) * mm});
            skArc(sketch, "E54.49.0", {"start": v(4.1, 64.31) * mm, "mid": v(3.92, 64.9) * mm, "end": v(3.36, 65.17) * mm});
            skLineSegment(sketch, "E54.49.1", {"start": v(3.97, 62.57) * mm, "end": v(4.1, 64.31) * mm});
            skArc(sketch, "E54.49.2", {"start": v(3.97, 62.57) * mm, "mid": v(4.29, 61.43) * mm, "end": v(4.7, 60.33) * mm});
            skArc(sketch, "E54.49.3", {"start": v(4.7, 60.33) * mm, "mid": v(4.95, 60) * mm, "end": v(5.33, 59.85) * mm});
            skLineSegment(sketch, "E54.49.4", {"start": v(5.33, 59.85) * mm, "end": v(5.72, 59.8) * mm});
            skLineSegment(sketch, "E54.49.5", {"start": v(6.12, 59.77) * mm, "end": v(5.72, 59.8) * mm});
            skArc(sketch, "E54.49.6", {"start": v(6.12, 59.77) * mm, "mid": v(6.52, 59.85) * mm, "end": v(6.83, 60.13) * mm});
            skArc(sketch, "E54.49.7", {"start": v(7.97, 62.19) * mm, "mid": v(7.44, 61.14) * mm, "end": v(6.83, 60.13) * mm});
            skLineSegment(sketch, "E54.49.8", {"start": v(7.97, 62.19) * mm, "end": v(8.15, 63.93) * mm});
            skArc(sketch, "E54.49.9", {"start": v(9.04, 64.63) * mm, "mid": v(8.45, 64.47) * mm, "end": v(8.15, 63.93) * mm});
            skArc(sketch, "E55.trimOffspring", {"start": v(3.36, 65.17) * mm, "mid": v(2.07, 65.22) * mm, "end": v(0.77, 65.25) * mm});
            skArc(sketch, "E56.trimOffspring", {"start": v(11.6, 64.22) * mm, "mid": v(10.33, 64.44) * mm, "end": v(9.04, 64.63) * mm});
            skArc(sketch, "E57.trimOffspring", {"start": v(19.66, 62.26) * mm, "mid": v(18.42, 62.63) * mm, "end": v(17.17, 62.98) * mm});
            skArc(sketch, "E58.trimOffspring", {"start": v(34.72, 55.38) * mm, "mid": v(33.61, 56.05) * mm, "end": v(32.5, 56.7) * mm});
            skArc(sketch, "E59.trimOffspring", {"start": v(27.4, 59.3) * mm, "mid": v(26.22, 59.82) * mm, "end": v(25.03, 60.32) * mm});
            skArc(sketch, "E60.trimOffspring", {"start": v(41.49, 50.59) * mm, "mid": v(40.47, 51.4) * mm, "end": v(39.44, 52.18) * mm});
            skArc(sketch, "E61.trimOffspring", {"start": v(47.6, 44.98) * mm, "mid": v(46.7, 45.9) * mm, "end": v(45.77, 46.82) * mm});
            skArc(sketch, "E62.trimOffspring", {"start": v(52.96, 38.66) * mm, "mid": v(52.18, 39.69) * mm, "end": v(51.37, 40.7) * mm});
            skArc(sketch, "E63.trimOffspring", {"start": v(57.49, 31.7) * mm, "mid": v(56.84, 32.83) * mm, "end": v(56.17, 33.94) * mm});
            skArc(sketch, "E64.trimOffspring", {"start": v(61.1, 24.24) * mm, "mid": v(60.6, 25.44) * mm, "end": v(60.08, 26.62) * mm});
            skArc(sketch, "E65.trimOffspring", {"start": v(63.76, 16.39) * mm, "mid": v(63.41, 17.64) * mm, "end": v(63.04, 18.88) * mm});
            skArc(sketch, "E66.trimOffspring", {"start": v(65.41, 8.26) * mm, "mid": v(65.22, 9.54) * mm, "end": v(65, 10.82) * mm});
            skArc(sketch, "E67.trimOffspring", {"start": v(66.03, -0.01) * mm, "mid": v(66, 1.29) * mm, "end": v(65.95, 2.58) * mm});
            skArc(sketch, "E68.trimOffspring", {"start": v(65.6, -8.3) * mm, "mid": v(65.74, -7) * mm, "end": v(65.85, -5.71) * mm});
            skArc(sketch, "E69.trimOffspring", {"start": v(64.15, -16.46) * mm, "mid": v(64.44, -15.2) * mm, "end": v(64.72, -13.93) * mm});
            skArc(sketch, "E70.trimOffspring", {"start": v(61.68, -24.37) * mm, "mid": v(62.13, -23.16) * mm, "end": v(62.56, -21.93) * mm});
            skArc(sketch, "E71.trimOffspring", {"start": v(58.24, -31.92) * mm, "mid": v(58.84, -30.77) * mm, "end": v(59.41, -29.6) * mm});
            skArc(sketch, "E72.trimOffspring", {"start": v(53.88, -38.97) * mm, "mid": v(54.62, -37.9) * mm, "end": v(55.33, -36.83) * mm});
            skArc(sketch, "E73.trimOffspring", {"start": v(48.67, -45.43) * mm, "mid": v(49.53, -44.46) * mm, "end": v(50.38, -43.48) * mm});
            skArc(sketch, "E74.trimOffspring", {"start": v(42.69, -51.17) * mm, "mid": v(43.67, -50.33) * mm, "end": v(44.63, -49.46) * mm});
            skArc(sketch, "E75.trimOffspring", {"start": v(36.04, -56.13) * mm, "mid": v(37.12, -55.4) * mm, "end": v(38.18, -54.67) * mm});
            skArc(sketch, "E76.trimOffspring", {"start": v(28.82, -60.2) * mm, "mid": v(29.98, -59.63) * mm, "end": v(31.13, -59.03) * mm});
            skArc(sketch, "E77.trimOffspring", {"start": v(21.14, -63.35) * mm, "mid": v(22.37, -62.92) * mm, "end": v(23.58, -62.47) * mm});
            skArc(sketch, "E78.trimOffspring", {"start": v(4.92, -66.64) * mm, "mid": v(6.21, -66.54) * mm, "end": v(7.5, -66.4) * mm});
            skArc(sketch, "E79.trimOffspring", {"start": v(-3.37, -66.74) * mm, "mid": v(-2.08, -66.8) * mm, "end": v(-0.78, -66.82) * mm});
            skArc(sketch, "E80.trimOffspring", {"start": v(13.13, -65.5) * mm, "mid": v(14.4, -65.24) * mm, "end": v(15.66, -64.94) * mm});
            skArc(sketch, "E81.trimOffspring", {"start": v(-19.67, -63.83) * mm, "mid": v(-18.43, -64.2) * mm, "end": v(-17.18, -64.56) * mm});
            skArc(sketch, "E82.trimOffspring", {"start": v(-27.42, -60.87) * mm, "mid": v(-26.23, -61.4) * mm, "end": v(-25.04, -61.9) * mm});
            skArc(sketch, "E83.trimOffspring", {"start": v(-34.73, -56.96) * mm, "mid": v(-33.62, -57.63) * mm, "end": v(-32.5, -58.28) * mm});
            skArc(sketch, "E84.trimOffspring", {"start": v(-41.5, -52.17) * mm, "mid": v(-40.48, -52.97) * mm, "end": v(-39.45, -53.75) * mm});
            skArc(sketch, "E85.trimOffspring", {"start": v(-52.97, -40.23) * mm, "mid": v(-52.19, -41.27) * mm, "end": v(-51.38, -42.28) * mm});
            skArc(sketch, "E86.trimOffspring", {"start": v(-47.6, -46.56) * mm, "mid": v(-46.7, -47.49) * mm, "end": v(-45.78, -48.4) * mm});
            skArc(sketch, "E87.trimOffspring", {"start": v(-57.5, -33.28) * mm, "mid": v(-56.85, -34.4) * mm, "end": v(-56.18, -35.52) * mm});
            skArc(sketch, "E88.trimOffspring", {"start": v(-61.12, -25.82) * mm, "mid": v(-60.61, -27.02) * mm, "end": v(-60.09, -28.2) * mm});
            skArc(sketch, "E89.trimOffspring", {"start": v(-63.77, -17.96) * mm, "mid": v(-63.42, -19.21) * mm, "end": v(-63.05, -20.45) * mm});
            skArc(sketch, "E90.trimOffspring", {"start": v(-65.42, -9.84) * mm, "mid": v(-65.23, -11.12) * mm, "end": v(-65.02, -12.4) * mm});
            skArc(sketch, "E91.trimOffspring", {"start": v(-66.04, -1.57) * mm, "mid": v(-66.01, -2.86) * mm, "end": v(-65.96, -4.16) * mm});
            skArc(sketch, "E92.trimOffspring", {"start": v(-65.62, 6.72) * mm, "mid": v(-65.75, 5.43) * mm, "end": v(-65.86, 4.13) * mm});
            skArc(sketch, "E93.trimOffspring", {"start": v(-64.16, 14.88) * mm, "mid": v(-64.45, 13.62) * mm, "end": v(-64.72, 12.35) * mm});
            skArc(sketch, "E94.trimOffspring", {"start": v(-61.69, 22.8) * mm, "mid": v(-62.14, 21.58) * mm, "end": v(-62.57, 20.36) * mm});
            skArc(sketch, "E95.trimOffspring", {"start": v(-58.25, 30.34) * mm, "mid": v(-58.85, 29.2) * mm, "end": v(-59.42, 28.03) * mm});
            skArc(sketch, "E96.trimOffspring", {"start": v(-53.89, 37.4) * mm, "mid": v(-54.63, 36.33) * mm, "end": v(-55.34, 35.25) * mm});
            skArc(sketch, "E97.trimOffspring", {"start": v(-48.68, 43.85) * mm, "mid": v(-49.54, 42.88) * mm, "end": v(-50.39, 41.9) * mm});
            skArc(sketch, "E98.trimOffspring", {"start": v(-42.7, 49.6) * mm, "mid": v(-43.68, 48.75) * mm, "end": v(-44.64, 47.88) * mm});
            skArc(sketch, "E99.trimOffspring", {"start": v(-36.05, 54.55) * mm, "mid": v(-37.12, 53.83) * mm, "end": v(-38.19, 53.1) * mm});
            skArc(sketch, "E100.trimOffspring", {"start": v(-28.83, 58.63) * mm, "mid": v(-29.99, 58.05) * mm, "end": v(-31.14, 57.45) * mm});
            skArc(sketch, "E101.trimOffspring", {"start": v(-21.15, 61.77) * mm, "mid": v(-22.37, 61.35) * mm, "end": v(-23.6, 60.9) * mm});
            skArc(sketch, "E102.trimOffspring", {"start": v(-13.14, 63.93) * mm, "mid": v(-14.41, 63.66) * mm, "end": v(-15.67, 63.37) * mm});
            skArc(sketch, "E103.trimOffspring", {"start": v(-11.61, -65.8) * mm, "mid": v(-10.34, -66.02) * mm, "end": v(-9.05, -66.2) * mm});
            skSolve(sketch);
        }
        {
            var Q0;
            Q0 = qSketchRegion(id + "F0", true);
            extrude(context, id + "F1", {"entities" : qUnion([Q0]), "depth" : 127 * mm});
        }
    });
